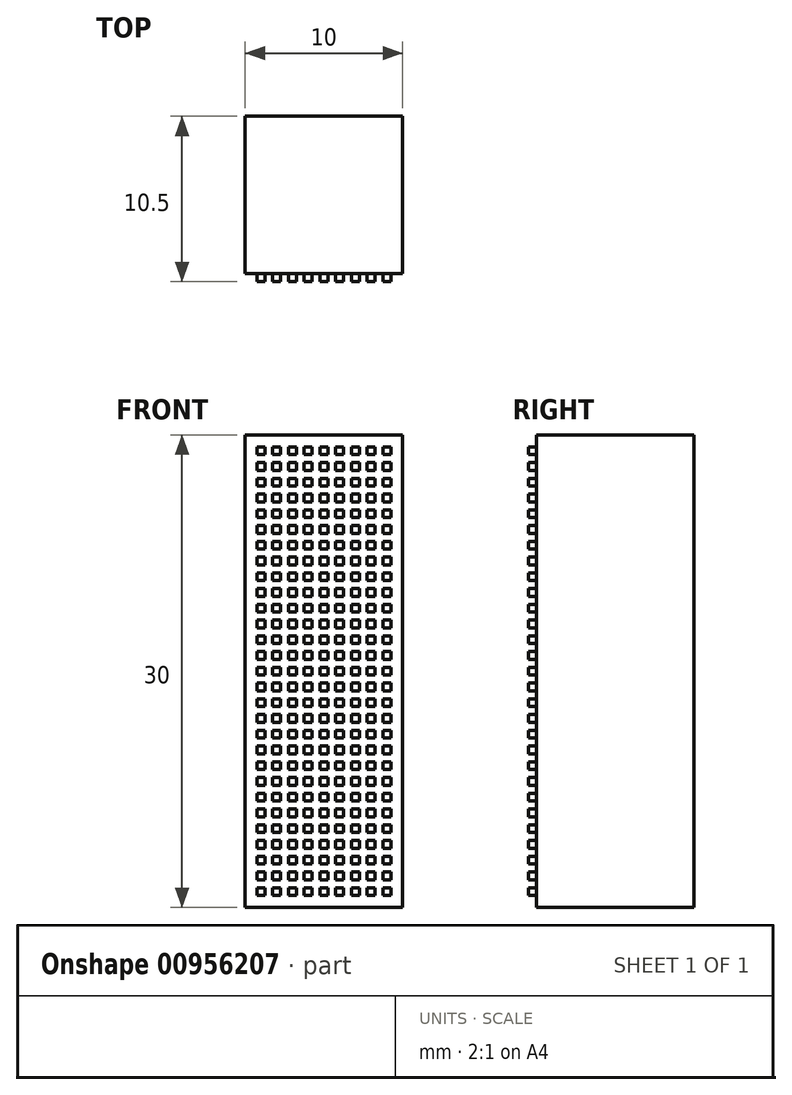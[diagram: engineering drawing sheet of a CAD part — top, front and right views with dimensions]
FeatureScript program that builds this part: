
annotation { "Feature Type Name" : "Feature", "Feature Type Description" : "" }
export const myFeature = defineFeature(function(context is Context, id is Id, definition is map)
    precondition{}
    {
        {
            var Q0;
            Q0=qCreatedBy(makeId("Front.planeOp"),FACE);
            var sketch = newSketch(context, id + "F0", { "sketchPlane" : qUnion([Q0])});
            skLineSegment(sketch, "E0.bottom", {"start": v(0.75, 0.75) * mm, "end": v(1.25, 0.75) * mm});
            skLineSegment(sketch, "E0.top", {"start": v(0.75, 1.25) * mm, "end": v(1.25, 1.25) * mm});
            skLineSegment(sketch, "E0.left", {"start": v(0.75, 0.75) * mm, "end": v(0.75, 1.25) * mm});
            skLineSegment(sketch, "E0.right", {"start": v(1.25, 0.75) * mm, "end": v(1.25, 1.25) * mm});
            skPoint(sketch, "E1", {"position": v(0, 0) * mm});
            skLineSegment(sketch, "E2.1.0.0", {"start": v(1.75, 0.75) * mm, "end": v(1.75, 1.25) * mm});
            skLineSegment(sketch, "E2.1.0.1", {"start": v(1.75, 0.75) * mm, "end": v(2.25, 0.75) * mm});
            skLineSegment(sketch, "E2.1.0.2", {"start": v(1.75, 1.25) * mm, "end": v(2.25, 1.25) * mm});
            skLineSegment(sketch, "E2.1.0.3", {"start": v(2.25, 0.75) * mm, "end": v(2.25, 1.25) * mm});
            skLineSegment(sketch, "E2.2.0.0", {"start": v(2.75, 0.75) * mm, "end": v(2.75, 1.25) * mm});
            skLineSegment(sketch, "E2.2.0.1", {"start": v(2.75, 0.75) * mm, "end": v(3.25, 0.75) * mm});
            skLineSegment(sketch, "E2.2.0.2", {"start": v(2.75, 1.25) * mm, "end": v(3.25, 1.25) * mm});
            skLineSegment(sketch, "E2.2.0.3", {"start": v(3.25, 0.75) * mm, "end": v(3.25, 1.25) * mm});
            skLineSegment(sketch, "E2.3.0.0", {"start": v(3.75, 0.75) * mm, "end": v(3.75, 1.25) * mm});
            skLineSegment(sketch, "E2.3.0.1", {"start": v(3.75, 0.75) * mm, "end": v(4.25, 0.75) * mm});
            skLineSegment(sketch, "E2.3.0.2", {"start": v(3.75, 1.25) * mm, "end": v(4.25, 1.25) * mm});
            skLineSegment(sketch, "E2.3.0.3", {"start": v(4.25, 0.75) * mm, "end": v(4.25, 1.25) * mm});
            skLineSegment(sketch, "E2.4.0.0", {"start": v(4.75, 0.75) * mm, "end": v(4.75, 1.25) * mm});
            skLineSegment(sketch, "E2.4.0.1", {"start": v(4.75, 0.75) * mm, "end": v(5.25, 0.75) * mm});
            skLineSegment(sketch, "E2.4.0.2", {"start": v(4.75, 1.25) * mm, "end": v(5.25, 1.25) * mm});
            skLineSegment(sketch, "E2.4.0.3", {"start": v(5.25, 0.75) * mm, "end": v(5.25, 1.25) * mm});
            skLineSegment(sketch, "E2.5.0.0", {"start": v(5.75, 0.75) * mm, "end": v(5.75, 1.25) * mm});
            skLineSegment(sketch, "E2.5.0.1", {"start": v(5.75, 0.75) * mm, "end": v(6.25, 0.75) * mm});
            skLineSegment(sketch, "E2.5.0.2", {"start": v(5.75, 1.25) * mm, "end": v(6.25, 1.25) * mm});
            skLineSegment(sketch, "E2.5.0.3", {"start": v(6.25, 0.75) * mm, "end": v(6.25, 1.25) * mm});
            skLineSegment(sketch, "E2.6.0.0", {"start": v(6.75, 0.75) * mm, "end": v(6.75, 1.25) * mm});
            skLineSegment(sketch, "E2.6.0.1", {"start": v(6.75, 0.75) * mm, "end": v(7.25, 0.75) * mm});
            skLineSegment(sketch, "E2.6.0.2", {"start": v(6.75, 1.25) * mm, "end": v(7.25, 1.25) * mm});
            skLineSegment(sketch, "E2.6.0.3", {"start": v(7.25, 0.75) * mm, "end": v(7.25, 1.25) * mm});
            skLineSegment(sketch, "E2.7.0.0", {"start": v(7.75, 0.75) * mm, "end": v(7.75, 1.25) * mm});
            skLineSegment(sketch, "E2.7.0.1", {"start": v(7.75, 0.75) * mm, "end": v(8.25, 0.75) * mm});
            skLineSegment(sketch, "E2.7.0.2", {"start": v(7.75, 1.25) * mm, "end": v(8.25, 1.25) * mm});
            skLineSegment(sketch, "E2.7.0.3", {"start": v(8.25, 0.75) * mm, "end": v(8.25, 1.25) * mm});
            skLineSegment(sketch, "E2.8.0.0", {"start": v(8.75, 0.75) * mm, "end": v(8.75, 1.25) * mm});
            skLineSegment(sketch, "E2.8.0.1", {"start": v(8.75, 0.75) * mm, "end": v(9.25, 0.75) * mm});
            skLineSegment(sketch, "E2.8.0.2", {"start": v(8.75, 1.25) * mm, "end": v(9.25, 1.25) * mm});
            skLineSegment(sketch, "E2.8.0.3", {"start": v(9.25, 0.75) * mm, "end": v(9.25, 1.25) * mm});
            skLineSegment(sketch, "E2.direction1", {"start": v(0.75, 0.75) * mm, "end": v(1.75, 0.75) * mm, "construction": true});
            skLineSegment(sketch, "E3.0.1.0", {"start": v(2.75, 2.25) * mm, "end": v(3.25, 2.25) * mm});
            skLineSegment(sketch, "E3.0.1.1", {"start": v(1.25, 1.75) * mm, "end": v(1.25, 2.25) * mm});
            skLineSegment(sketch, "E3.0.1.2", {"start": v(1.75, 2.25) * mm, "end": v(2.25, 2.25) * mm});
            skLineSegment(sketch, "E3.0.1.3", {"start": v(0.75, 1.75) * mm, "end": v(0.75, 2.25) * mm});
            skLineSegment(sketch, "E3.0.1.4", {"start": v(5.75, 2.25) * mm, "end": v(6.25, 2.25) * mm});
            skLineSegment(sketch, "E3.0.1.5", {"start": v(5.25, 1.75) * mm, "end": v(5.25, 2.25) * mm});
            skLineSegment(sketch, "E3.0.1.6", {"start": v(7.75, 1.75) * mm, "end": v(7.75, 2.25) * mm});
            skLineSegment(sketch, "E3.0.1.7", {"start": v(6.75, 1.75) * mm, "end": v(7.25, 1.75) * mm});
            skLineSegment(sketch, "E3.0.1.8", {"start": v(2.75, 1.75) * mm, "end": v(3.25, 1.75) * mm});
            skLineSegment(sketch, "E3.0.1.9", {"start": v(1.75, 1.75) * mm, "end": v(1.75, 2.25) * mm});
            skLineSegment(sketch, "E3.0.1.10", {"start": v(8.75, 1.75) * mm, "end": v(8.75, 2.25) * mm});
            skLineSegment(sketch, "E3.0.1.11", {"start": v(5.75, 1.75) * mm, "end": v(5.75, 2.25) * mm});
            skLineSegment(sketch, "E3.0.1.12", {"start": v(7.25, 1.75) * mm, "end": v(7.25, 2.25) * mm});
            skLineSegment(sketch, "E3.0.1.13", {"start": v(4.25, 1.75) * mm, "end": v(4.25, 2.25) * mm});
            skLineSegment(sketch, "E3.0.1.14", {"start": v(7.75, 2.25) * mm, "end": v(8.25, 2.25) * mm});
            skLineSegment(sketch, "E3.0.1.15", {"start": v(3.75, 1.75) * mm, "end": v(3.75, 2.25) * mm});
            skLineSegment(sketch, "E3.0.1.16", {"start": v(0.75, 2.25) * mm, "end": v(1.25, 2.25) * mm});
            skLineSegment(sketch, "E3.0.1.17", {"start": v(3.75, 1.75) * mm, "end": v(4.25, 1.75) * mm});
            skLineSegment(sketch, "E3.0.1.18", {"start": v(3.75, 2.25) * mm, "end": v(4.25, 2.25) * mm});
            skLineSegment(sketch, "E3.0.1.19", {"start": v(4.75, 1.75) * mm, "end": v(5.25, 1.75) * mm});
            skLineSegment(sketch, "E3.0.1.20", {"start": v(3.25, 1.75) * mm, "end": v(3.25, 2.25) * mm});
            skLineSegment(sketch, "E3.0.1.21", {"start": v(8.75, 1.75) * mm, "end": v(9.25, 1.75) * mm});
            skLineSegment(sketch, "E3.0.1.22", {"start": v(4.75, 2.25) * mm, "end": v(5.25, 2.25) * mm});
            skLineSegment(sketch, "E3.0.1.23", {"start": v(8.75, 2.25) * mm, "end": v(9.25, 2.25) * mm});
            skLineSegment(sketch, "E3.0.1.24", {"start": v(6.75, 1.75) * mm, "end": v(6.75, 2.25) * mm});
            skLineSegment(sketch, "E3.0.1.25", {"start": v(2.75, 1.75) * mm, "end": v(2.75, 2.25) * mm});
            skLineSegment(sketch, "E3.0.1.26", {"start": v(0.75, 1.75) * mm, "end": v(1.75, 1.75) * mm, "construction": true});
            skLineSegment(sketch, "E3.0.1.27", {"start": v(6.25, 1.75) * mm, "end": v(6.25, 2.25) * mm});
            skLineSegment(sketch, "E3.0.1.28", {"start": v(6.75, 2.25) * mm, "end": v(7.25, 2.25) * mm});
            skLineSegment(sketch, "E3.0.1.29", {"start": v(2.25, 1.75) * mm, "end": v(2.25, 2.25) * mm});
            skLineSegment(sketch, "E3.0.1.30", {"start": v(8.25, 1.75) * mm, "end": v(8.25, 2.25) * mm});
            skLineSegment(sketch, "E3.0.1.31", {"start": v(1.75, 1.75) * mm, "end": v(2.25, 1.75) * mm});
            skLineSegment(sketch, "E3.0.1.32", {"start": v(9.25, 1.75) * mm, "end": v(9.25, 2.25) * mm});
            skLineSegment(sketch, "E3.0.1.33", {"start": v(7.75, 1.75) * mm, "end": v(8.25, 1.75) * mm});
            skLineSegment(sketch, "E3.0.1.34", {"start": v(5.75, 1.75) * mm, "end": v(6.25, 1.75) * mm});
            skLineSegment(sketch, "E3.0.1.35", {"start": v(4.75, 1.75) * mm, "end": v(4.75, 2.25) * mm});
            skLineSegment(sketch, "E3.0.1.36", {"start": v(0.75, 1.75) * mm, "end": v(1.25, 1.75) * mm});
            skLineSegment(sketch, "E3.0.2.0", {"start": v(2.75, 3.25) * mm, "end": v(3.25, 3.25) * mm});
            skLineSegment(sketch, "E3.0.2.1", {"start": v(1.25, 2.75) * mm, "end": v(1.25, 3.25) * mm});
            skLineSegment(sketch, "E3.0.2.2", {"start": v(1.75, 3.25) * mm, "end": v(2.25, 3.25) * mm});
            skLineSegment(sketch, "E3.0.2.3", {"start": v(0.75, 2.75) * mm, "end": v(0.75, 3.25) * mm});
            skLineSegment(sketch, "E3.0.2.4", {"start": v(5.75, 3.25) * mm, "end": v(6.25, 3.25) * mm});
            skLineSegment(sketch, "E3.0.2.5", {"start": v(5.25, 2.75) * mm, "end": v(5.25, 3.25) * mm});
            skLineSegment(sketch, "E3.0.2.6", {"start": v(7.75, 2.75) * mm, "end": v(7.75, 3.25) * mm});
            skLineSegment(sketch, "E3.0.2.7", {"start": v(6.75, 2.75) * mm, "end": v(7.25, 2.75) * mm});
            skLineSegment(sketch, "E3.0.2.8", {"start": v(2.75, 2.75) * mm, "end": v(3.25, 2.75) * mm});
            skLineSegment(sketch, "E3.0.2.9", {"start": v(1.75, 2.75) * mm, "end": v(1.75, 3.25) * mm});
            skLineSegment(sketch, "E3.0.2.10", {"start": v(8.75, 2.75) * mm, "end": v(8.75, 3.25) * mm});
            skLineSegment(sketch, "E3.0.2.11", {"start": v(5.75, 2.75) * mm, "end": v(5.75, 3.25) * mm});
            skLineSegment(sketch, "E3.0.2.12", {"start": v(7.25, 2.75) * mm, "end": v(7.25, 3.25) * mm});
            skLineSegment(sketch, "E3.0.2.13", {"start": v(4.25, 2.75) * mm, "end": v(4.25, 3.25) * mm});
            skLineSegment(sketch, "E3.0.2.14", {"start": v(7.75, 3.25) * mm, "end": v(8.25, 3.25) * mm});
            skLineSegment(sketch, "E3.0.2.15", {"start": v(3.75, 2.75) * mm, "end": v(3.75, 3.25) * mm});
            skLineSegment(sketch, "E3.0.2.16", {"start": v(0.75, 3.25) * mm, "end": v(1.25, 3.25) * mm});
            skLineSegment(sketch, "E3.0.2.17", {"start": v(3.75, 2.75) * mm, "end": v(4.25, 2.75) * mm});
            skLineSegment(sketch, "E3.0.2.18", {"start": v(3.75, 3.25) * mm, "end": v(4.25, 3.25) * mm});
            skLineSegment(sketch, "E3.0.2.19", {"start": v(4.75, 2.75) * mm, "end": v(5.25, 2.75) * mm});
            skLineSegment(sketch, "E3.0.2.20", {"start": v(3.25, 2.75) * mm, "end": v(3.25, 3.25) * mm});
            skLineSegment(sketch, "E3.0.2.21", {"start": v(8.75, 2.75) * mm, "end": v(9.25, 2.75) * mm});
            skLineSegment(sketch, "E3.0.2.22", {"start": v(4.75, 3.25) * mm, "end": v(5.25, 3.25) * mm});
            skLineSegment(sketch, "E3.0.2.23", {"start": v(8.75, 3.25) * mm, "end": v(9.25, 3.25) * mm});
            skLineSegment(sketch, "E3.0.2.24", {"start": v(6.75, 2.75) * mm, "end": v(6.75, 3.25) * mm});
            skLineSegment(sketch, "E3.0.2.25", {"start": v(2.75, 2.75) * mm, "end": v(2.75, 3.25) * mm});
            skLineSegment(sketch, "E3.0.2.26", {"start": v(0.75, 2.75) * mm, "end": v(1.75, 2.75) * mm, "construction": true});
            skLineSegment(sketch, "E3.0.2.27", {"start": v(6.25, 2.75) * mm, "end": v(6.25, 3.25) * mm});
            skLineSegment(sketch, "E3.0.2.28", {"start": v(6.75, 3.25) * mm, "end": v(7.25, 3.25) * mm});
            skLineSegment(sketch, "E3.0.2.29", {"start": v(2.25, 2.75) * mm, "end": v(2.25, 3.25) * mm});
            skLineSegment(sketch, "E3.0.2.30", {"start": v(8.25, 2.75) * mm, "end": v(8.25, 3.25) * mm});
            skLineSegment(sketch, "E3.0.2.31", {"start": v(1.75, 2.75) * mm, "end": v(2.25, 2.75) * mm});
            skLineSegment(sketch, "E3.0.2.32", {"start": v(9.25, 2.75) * mm, "end": v(9.25, 3.25) * mm});
            skLineSegment(sketch, "E3.0.2.33", {"start": v(7.75, 2.75) * mm, "end": v(8.25, 2.75) * mm});
            skLineSegment(sketch, "E3.0.2.34", {"start": v(5.75, 2.75) * mm, "end": v(6.25, 2.75) * mm});
            skLineSegment(sketch, "E3.0.2.35", {"start": v(4.75, 2.75) * mm, "end": v(4.75, 3.25) * mm});
            skLineSegment(sketch, "E3.0.2.36", {"start": v(0.75, 2.75) * mm, "end": v(1.25, 2.75) * mm});
            skLineSegment(sketch, "E3.0.3.0", {"start": v(2.75, 4.25) * mm, "end": v(3.25, 4.25) * mm});
            skLineSegment(sketch, "E3.0.3.1", {"start": v(1.25, 3.75) * mm, "end": v(1.25, 4.25) * mm});
            skLineSegment(sketch, "E3.0.3.2", {"start": v(1.75, 4.25) * mm, "end": v(2.25, 4.25) * mm});
            skLineSegment(sketch, "E3.0.3.3", {"start": v(0.75, 3.75) * mm, "end": v(0.75, 4.25) * mm});
            skLineSegment(sketch, "E3.0.3.4", {"start": v(5.75, 4.25) * mm, "end": v(6.25, 4.25) * mm});
            skLineSegment(sketch, "E3.0.3.5", {"start": v(5.25, 3.75) * mm, "end": v(5.25, 4.25) * mm});
            skLineSegment(sketch, "E3.0.3.6", {"start": v(7.75, 3.75) * mm, "end": v(7.75, 4.25) * mm});
            skLineSegment(sketch, "E3.0.3.7", {"start": v(6.75, 3.75) * mm, "end": v(7.25, 3.75) * mm});
            skLineSegment(sketch, "E3.0.3.8", {"start": v(2.75, 3.75) * mm, "end": v(3.25, 3.75) * mm});
            skLineSegment(sketch, "E3.0.3.9", {"start": v(1.75, 3.75) * mm, "end": v(1.75, 4.25) * mm});
            skLineSegment(sketch, "E3.0.3.10", {"start": v(8.75, 3.75) * mm, "end": v(8.75, 4.25) * mm});
            skLineSegment(sketch, "E3.0.3.11", {"start": v(5.75, 3.75) * mm, "end": v(5.75, 4.25) * mm});
            skLineSegment(sketch, "E3.0.3.12", {"start": v(7.25, 3.75) * mm, "end": v(7.25, 4.25) * mm});
            skLineSegment(sketch, "E3.0.3.13", {"start": v(4.25, 3.75) * mm, "end": v(4.25, 4.25) * mm});
            skLineSegment(sketch, "E3.0.3.14", {"start": v(7.75, 4.25) * mm, "end": v(8.25, 4.25) * mm});
            skLineSegment(sketch, "E3.0.3.15", {"start": v(3.75, 3.75) * mm, "end": v(3.75, 4.25) * mm});
            skLineSegment(sketch, "E3.0.3.16", {"start": v(0.75, 4.25) * mm, "end": v(1.25, 4.25) * mm});
            skLineSegment(sketch, "E3.0.3.17", {"start": v(3.75, 3.75) * mm, "end": v(4.25, 3.75) * mm});
            skLineSegment(sketch, "E3.0.3.18", {"start": v(3.75, 4.25) * mm, "end": v(4.25, 4.25) * mm});
            skLineSegment(sketch, "E3.0.3.19", {"start": v(4.75, 3.75) * mm, "end": v(5.25, 3.75) * mm});
            skLineSegment(sketch, "E3.0.3.20", {"start": v(3.25, 3.75) * mm, "end": v(3.25, 4.25) * mm});
            skLineSegment(sketch, "E3.0.3.21", {"start": v(8.75, 3.75) * mm, "end": v(9.25, 3.75) * mm});
            skLineSegment(sketch, "E3.0.3.22", {"start": v(4.75, 4.25) * mm, "end": v(5.25, 4.25) * mm});
            skLineSegment(sketch, "E3.0.3.23", {"start": v(8.75, 4.25) * mm, "end": v(9.25, 4.25) * mm});
            skLineSegment(sketch, "E3.0.3.24", {"start": v(6.75, 3.75) * mm, "end": v(6.75, 4.25) * mm});
            skLineSegment(sketch, "E3.0.3.25", {"start": v(2.75, 3.75) * mm, "end": v(2.75, 4.25) * mm});
            skLineSegment(sketch, "E3.0.3.26", {"start": v(0.75, 3.75) * mm, "end": v(1.75, 3.75) * mm, "construction": true});
            skLineSegment(sketch, "E3.0.3.27", {"start": v(6.25, 3.75) * mm, "end": v(6.25, 4.25) * mm});
            skLineSegment(sketch, "E3.0.3.28", {"start": v(6.75, 4.25) * mm, "end": v(7.25, 4.25) * mm});
            skLineSegment(sketch, "E3.0.3.29", {"start": v(2.25, 3.75) * mm, "end": v(2.25, 4.25) * mm});
            skLineSegment(sketch, "E3.0.3.30", {"start": v(8.25, 3.75) * mm, "end": v(8.25, 4.25) * mm});
            skLineSegment(sketch, "E3.0.3.31", {"start": v(1.75, 3.75) * mm, "end": v(2.25, 3.75) * mm});
            skLineSegment(sketch, "E3.0.3.32", {"start": v(9.25, 3.75) * mm, "end": v(9.25, 4.25) * mm});
            skLineSegment(sketch, "E3.0.3.33", {"start": v(7.75, 3.75) * mm, "end": v(8.25, 3.75) * mm});
            skLineSegment(sketch, "E3.0.3.34", {"start": v(5.75, 3.75) * mm, "end": v(6.25, 3.75) * mm});
            skLineSegment(sketch, "E3.0.3.35", {"start": v(4.75, 3.75) * mm, "end": v(4.75, 4.25) * mm});
            skLineSegment(sketch, "E3.0.3.36", {"start": v(0.75, 3.75) * mm, "end": v(1.25, 3.75) * mm});
            skLineSegment(sketch, "E3.0.4.0", {"start": v(2.75, 5.25) * mm, "end": v(3.25, 5.25) * mm});
            skLineSegment(sketch, "E3.0.4.1", {"start": v(1.25, 4.75) * mm, "end": v(1.25, 5.25) * mm});
            skLineSegment(sketch, "E3.0.4.2", {"start": v(1.75, 5.25) * mm, "end": v(2.25, 5.25) * mm});
            skLineSegment(sketch, "E3.0.4.3", {"start": v(0.75, 4.75) * mm, "end": v(0.75, 5.25) * mm});
            skLineSegment(sketch, "E3.0.4.4", {"start": v(5.75, 5.25) * mm, "end": v(6.25, 5.25) * mm});
            skLineSegment(sketch, "E3.0.4.5", {"start": v(5.25, 4.75) * mm, "end": v(5.25, 5.25) * mm});
            skLineSegment(sketch, "E3.0.4.6", {"start": v(7.75, 4.75) * mm, "end": v(7.75, 5.25) * mm});
            skLineSegment(sketch, "E3.0.4.7", {"start": v(6.75, 4.75) * mm, "end": v(7.25, 4.75) * mm});
            skLineSegment(sketch, "E3.0.4.8", {"start": v(2.75, 4.75) * mm, "end": v(3.25, 4.75) * mm});
            skLineSegment(sketch, "E3.0.4.9", {"start": v(1.75, 4.75) * mm, "end": v(1.75, 5.25) * mm});
            skLineSegment(sketch, "E3.0.4.10", {"start": v(8.75, 4.75) * mm, "end": v(8.75, 5.25) * mm});
            skLineSegment(sketch, "E3.0.4.11", {"start": v(5.75, 4.75) * mm, "end": v(5.75, 5.25) * mm});
            skLineSegment(sketch, "E3.0.4.12", {"start": v(7.25, 4.75) * mm, "end": v(7.25, 5.25) * mm});
            skLineSegment(sketch, "E3.0.4.13", {"start": v(4.25, 4.75) * mm, "end": v(4.25, 5.25) * mm});
            skLineSegment(sketch, "E3.0.4.14", {"start": v(7.75, 5.25) * mm, "end": v(8.25, 5.25) * mm});
            skLineSegment(sketch, "E3.0.4.15", {"start": v(3.75, 4.75) * mm, "end": v(3.75, 5.25) * mm});
            skLineSegment(sketch, "E3.0.4.16", {"start": v(0.75, 5.25) * mm, "end": v(1.25, 5.25) * mm});
            skLineSegment(sketch, "E3.0.4.17", {"start": v(3.75, 4.75) * mm, "end": v(4.25, 4.75) * mm});
            skLineSegment(sketch, "E3.0.4.18", {"start": v(3.75, 5.25) * mm, "end": v(4.25, 5.25) * mm});
            skLineSegment(sketch, "E3.0.4.19", {"start": v(4.75, 4.75) * mm, "end": v(5.25, 4.75) * mm});
            skLineSegment(sketch, "E3.0.4.20", {"start": v(3.25, 4.75) * mm, "end": v(3.25, 5.25) * mm});
            skLineSegment(sketch, "E3.0.4.21", {"start": v(8.75, 4.75) * mm, "end": v(9.25, 4.75) * mm});
            skLineSegment(sketch, "E3.0.4.22", {"start": v(4.75, 5.25) * mm, "end": v(5.25, 5.25) * mm});
            skLineSegment(sketch, "E3.0.4.23", {"start": v(8.75, 5.25) * mm, "end": v(9.25, 5.25) * mm});
            skLineSegment(sketch, "E3.0.4.24", {"start": v(6.75, 4.75) * mm, "end": v(6.75, 5.25) * mm});
            skLineSegment(sketch, "E3.0.4.25", {"start": v(2.75, 4.75) * mm, "end": v(2.75, 5.25) * mm});
            skLineSegment(sketch, "E3.0.4.26", {"start": v(0.75, 4.75) * mm, "end": v(1.75, 4.75) * mm, "construction": true});
            skLineSegment(sketch, "E3.0.4.27", {"start": v(6.25, 4.75) * mm, "end": v(6.25, 5.25) * mm});
            skLineSegment(sketch, "E3.0.4.28", {"start": v(6.75, 5.25) * mm, "end": v(7.25, 5.25) * mm});
            skLineSegment(sketch, "E3.0.4.29", {"start": v(2.25, 4.75) * mm, "end": v(2.25, 5.25) * mm});
            skLineSegment(sketch, "E3.0.4.30", {"start": v(8.25, 4.75) * mm, "end": v(8.25, 5.25) * mm});
            skLineSegment(sketch, "E3.0.4.31", {"start": v(1.75, 4.75) * mm, "end": v(2.25, 4.75) * mm});
            skLineSegment(sketch, "E3.0.4.32", {"start": v(9.25, 4.75) * mm, "end": v(9.25, 5.25) * mm});
            skLineSegment(sketch, "E3.0.4.33", {"start": v(7.75, 4.75) * mm, "end": v(8.25, 4.75) * mm});
            skLineSegment(sketch, "E3.0.4.34", {"start": v(5.75, 4.75) * mm, "end": v(6.25, 4.75) * mm});
            skLineSegment(sketch, "E3.0.4.35", {"start": v(4.75, 4.75) * mm, "end": v(4.75, 5.25) * mm});
            skLineSegment(sketch, "E3.0.4.36", {"start": v(0.75, 4.75) * mm, "end": v(1.25, 4.75) * mm});
            skLineSegment(sketch, "E3.0.5.0", {"start": v(2.75, 6.25) * mm, "end": v(3.25, 6.25) * mm});
            skLineSegment(sketch, "E3.0.5.1", {"start": v(1.25, 5.75) * mm, "end": v(1.25, 6.25) * mm});
            skLineSegment(sketch, "E3.0.5.2", {"start": v(1.75, 6.25) * mm, "end": v(2.25, 6.25) * mm});
            skLineSegment(sketch, "E3.0.5.3", {"start": v(0.75, 5.75) * mm, "end": v(0.75, 6.25) * mm});
            skLineSegment(sketch, "E3.0.5.4", {"start": v(5.75, 6.25) * mm, "end": v(6.25, 6.25) * mm});
            skLineSegment(sketch, "E3.0.5.5", {"start": v(5.25, 5.75) * mm, "end": v(5.25, 6.25) * mm});
            skLineSegment(sketch, "E3.0.5.6", {"start": v(7.75, 5.75) * mm, "end": v(7.75, 6.25) * mm});
            skLineSegment(sketch, "E3.0.5.7", {"start": v(6.75, 5.75) * mm, "end": v(7.25, 5.75) * mm});
            skLineSegment(sketch, "E3.0.5.8", {"start": v(2.75, 5.75) * mm, "end": v(3.25, 5.75) * mm});
            skLineSegment(sketch, "E3.0.5.9", {"start": v(1.75, 5.75) * mm, "end": v(1.75, 6.25) * mm});
            skLineSegment(sketch, "E3.0.5.10", {"start": v(8.75, 5.75) * mm, "end": v(8.75, 6.25) * mm});
            skLineSegment(sketch, "E3.0.5.11", {"start": v(5.75, 5.75) * mm, "end": v(5.75, 6.25) * mm});
            skLineSegment(sketch, "E3.0.5.12", {"start": v(7.25, 5.75) * mm, "end": v(7.25, 6.25) * mm});
            skLineSegment(sketch, "E3.0.5.13", {"start": v(4.25, 5.75) * mm, "end": v(4.25, 6.25) * mm});
            skLineSegment(sketch, "E3.0.5.14", {"start": v(7.75, 6.25) * mm, "end": v(8.25, 6.25) * mm});
            skLineSegment(sketch, "E3.0.5.15", {"start": v(3.75, 5.75) * mm, "end": v(3.75, 6.25) * mm});
            skLineSegment(sketch, "E3.0.5.16", {"start": v(0.75, 6.25) * mm, "end": v(1.25, 6.25) * mm});
            skLineSegment(sketch, "E3.0.5.17", {"start": v(3.75, 5.75) * mm, "end": v(4.25, 5.75) * mm});
            skLineSegment(sketch, "E3.0.5.18", {"start": v(3.75, 6.25) * mm, "end": v(4.25, 6.25) * mm});
            skLineSegment(sketch, "E3.0.5.19", {"start": v(4.75, 5.75) * mm, "end": v(5.25, 5.75) * mm});
            skLineSegment(sketch, "E3.0.5.20", {"start": v(3.25, 5.75) * mm, "end": v(3.25, 6.25) * mm});
            skLineSegment(sketch, "E3.0.5.21", {"start": v(8.75, 5.75) * mm, "end": v(9.25, 5.75) * mm});
            skLineSegment(sketch, "E3.0.5.22", {"start": v(4.75, 6.25) * mm, "end": v(5.25, 6.25) * mm});
            skLineSegment(sketch, "E3.0.5.23", {"start": v(8.75, 6.25) * mm, "end": v(9.25, 6.25) * mm});
            skLineSegment(sketch, "E3.0.5.24", {"start": v(6.75, 5.75) * mm, "end": v(6.75, 6.25) * mm});
            skLineSegment(sketch, "E3.0.5.25", {"start": v(2.75, 5.75) * mm, "end": v(2.75, 6.25) * mm});
            skLineSegment(sketch, "E3.0.5.26", {"start": v(0.75, 5.75) * mm, "end": v(1.75, 5.75) * mm, "construction": true});
            skLineSegment(sketch, "E3.0.5.27", {"start": v(6.25, 5.75) * mm, "end": v(6.25, 6.25) * mm});
            skLineSegment(sketch, "E3.0.5.28", {"start": v(6.75, 6.25) * mm, "end": v(7.25, 6.25) * mm});
            skLineSegment(sketch, "E3.0.5.29", {"start": v(2.25, 5.75) * mm, "end": v(2.25, 6.25) * mm});
            skLineSegment(sketch, "E3.0.5.30", {"start": v(8.25, 5.75) * mm, "end": v(8.25, 6.25) * mm});
            skLineSegment(sketch, "E3.0.5.31", {"start": v(1.75, 5.75) * mm, "end": v(2.25, 5.75) * mm});
            skLineSegment(sketch, "E3.0.5.32", {"start": v(9.25, 5.75) * mm, "end": v(9.25, 6.25) * mm});
            skLineSegment(sketch, "E3.0.5.33", {"start": v(7.75, 5.75) * mm, "end": v(8.25, 5.75) * mm});
            skLineSegment(sketch, "E3.0.5.34", {"start": v(5.75, 5.75) * mm, "end": v(6.25, 5.75) * mm});
            skLineSegment(sketch, "E3.0.5.35", {"start": v(4.75, 5.75) * mm, "end": v(4.75, 6.25) * mm});
            skLineSegment(sketch, "E3.0.5.36", {"start": v(0.75, 5.75) * mm, "end": v(1.25, 5.75) * mm});
            skLineSegment(sketch, "E3.0.6.0", {"start": v(2.75, 7.25) * mm, "end": v(3.25, 7.25) * mm});
            skLineSegment(sketch, "E3.0.6.1", {"start": v(1.25, 6.75) * mm, "end": v(1.25, 7.25) * mm});
            skLineSegment(sketch, "E3.0.6.2", {"start": v(1.75, 7.25) * mm, "end": v(2.25, 7.25) * mm});
            skLineSegment(sketch, "E3.0.6.3", {"start": v(0.75, 6.75) * mm, "end": v(0.75, 7.25) * mm});
            skLineSegment(sketch, "E3.0.6.4", {"start": v(5.75, 7.25) * mm, "end": v(6.25, 7.25) * mm});
            skLineSegment(sketch, "E3.0.6.5", {"start": v(5.25, 6.75) * mm, "end": v(5.25, 7.25) * mm});
            skLineSegment(sketch, "E3.0.6.6", {"start": v(7.75, 6.75) * mm, "end": v(7.75, 7.25) * mm});
            skLineSegment(sketch, "E3.0.6.7", {"start": v(6.75, 6.75) * mm, "end": v(7.25, 6.75) * mm});
            skLineSegment(sketch, "E3.0.6.8", {"start": v(2.75, 6.75) * mm, "end": v(3.25, 6.75) * mm});
            skLineSegment(sketch, "E3.0.6.9", {"start": v(1.75, 6.75) * mm, "end": v(1.75, 7.25) * mm});
            skLineSegment(sketch, "E3.0.6.10", {"start": v(8.75, 6.75) * mm, "end": v(8.75, 7.25) * mm});
            skLineSegment(sketch, "E3.0.6.11", {"start": v(5.75, 6.75) * mm, "end": v(5.75, 7.25) * mm});
            skLineSegment(sketch, "E3.0.6.12", {"start": v(7.25, 6.75) * mm, "end": v(7.25, 7.25) * mm});
            skLineSegment(sketch, "E3.0.6.13", {"start": v(4.25, 6.75) * mm, "end": v(4.25, 7.25) * mm});
            skLineSegment(sketch, "E3.0.6.14", {"start": v(7.75, 7.25) * mm, "end": v(8.25, 7.25) * mm});
            skLineSegment(sketch, "E3.0.6.15", {"start": v(3.75, 6.75) * mm, "end": v(3.75, 7.25) * mm});
            skLineSegment(sketch, "E3.0.6.16", {"start": v(0.75, 7.25) * mm, "end": v(1.25, 7.25) * mm});
            skLineSegment(sketch, "E3.0.6.17", {"start": v(3.75, 6.75) * mm, "end": v(4.25, 6.75) * mm});
            skLineSegment(sketch, "E3.0.6.18", {"start": v(3.75, 7.25) * mm, "end": v(4.25, 7.25) * mm});
            skLineSegment(sketch, "E3.0.6.19", {"start": v(4.75, 6.75) * mm, "end": v(5.25, 6.75) * mm});
            skLineSegment(sketch, "E3.0.6.20", {"start": v(3.25, 6.75) * mm, "end": v(3.25, 7.25) * mm});
            skLineSegment(sketch, "E3.0.6.21", {"start": v(8.75, 6.75) * mm, "end": v(9.25, 6.75) * mm});
            skLineSegment(sketch, "E3.0.6.22", {"start": v(4.75, 7.25) * mm, "end": v(5.25, 7.25) * mm});
            skLineSegment(sketch, "E3.0.6.23", {"start": v(8.75, 7.25) * mm, "end": v(9.25, 7.25) * mm});
            skLineSegment(sketch, "E3.0.6.24", {"start": v(6.75, 6.75) * mm, "end": v(6.75, 7.25) * mm});
            skLineSegment(sketch, "E3.0.6.25", {"start": v(2.75, 6.75) * mm, "end": v(2.75, 7.25) * mm});
            skLineSegment(sketch, "E3.0.6.26", {"start": v(0.75, 6.75) * mm, "end": v(1.75, 6.75) * mm, "construction": true});
            skLineSegment(sketch, "E3.0.6.27", {"start": v(6.25, 6.75) * mm, "end": v(6.25, 7.25) * mm});
            skLineSegment(sketch, "E3.0.6.28", {"start": v(6.75, 7.25) * mm, "end": v(7.25, 7.25) * mm});
            skLineSegment(sketch, "E3.0.6.29", {"start": v(2.25, 6.75) * mm, "end": v(2.25, 7.25) * mm});
            skLineSegment(sketch, "E3.0.6.30", {"start": v(8.25, 6.75) * mm, "end": v(8.25, 7.25) * mm});
            skLineSegment(sketch, "E3.0.6.31", {"start": v(1.75, 6.75) * mm, "end": v(2.25, 6.75) * mm});
            skLineSegment(sketch, "E3.0.6.32", {"start": v(9.25, 6.75) * mm, "end": v(9.25, 7.25) * mm});
            skLineSegment(sketch, "E3.0.6.33", {"start": v(7.75, 6.75) * mm, "end": v(8.25, 6.75) * mm});
            skLineSegment(sketch, "E3.0.6.34", {"start": v(5.75, 6.75) * mm, "end": v(6.25, 6.75) * mm});
            skLineSegment(sketch, "E3.0.6.35", {"start": v(4.75, 6.75) * mm, "end": v(4.75, 7.25) * mm});
            skLineSegment(sketch, "E3.0.6.36", {"start": v(0.75, 6.75) * mm, "end": v(1.25, 6.75) * mm});
            skLineSegment(sketch, "E3.0.7.0", {"start": v(2.75, 8.25) * mm, "end": v(3.25, 8.25) * mm});
            skLineSegment(sketch, "E3.0.7.1", {"start": v(1.25, 7.75) * mm, "end": v(1.25, 8.25) * mm});
            skLineSegment(sketch, "E3.0.7.2", {"start": v(1.75, 8.25) * mm, "end": v(2.25, 8.25) * mm});
            skLineSegment(sketch, "E3.0.7.3", {"start": v(0.75, 7.75) * mm, "end": v(0.75, 8.25) * mm});
            skLineSegment(sketch, "E3.0.7.4", {"start": v(5.75, 8.25) * mm, "end": v(6.25, 8.25) * mm});
            skLineSegment(sketch, "E3.0.7.5", {"start": v(5.25, 7.75) * mm, "end": v(5.25, 8.25) * mm});
            skLineSegment(sketch, "E3.0.7.6", {"start": v(7.75, 7.75) * mm, "end": v(7.75, 8.25) * mm});
            skLineSegment(sketch, "E3.0.7.7", {"start": v(6.75, 7.75) * mm, "end": v(7.25, 7.75) * mm});
            skLineSegment(sketch, "E3.0.7.8", {"start": v(2.75, 7.75) * mm, "end": v(3.25, 7.75) * mm});
            skLineSegment(sketch, "E3.0.7.9", {"start": v(1.75, 7.75) * mm, "end": v(1.75, 8.25) * mm});
            skLineSegment(sketch, "E3.0.7.10", {"start": v(8.75, 7.75) * mm, "end": v(8.75, 8.25) * mm});
            skLineSegment(sketch, "E3.0.7.11", {"start": v(5.75, 7.75) * mm, "end": v(5.75, 8.25) * mm});
            skLineSegment(sketch, "E3.0.7.12", {"start": v(7.25, 7.75) * mm, "end": v(7.25, 8.25) * mm});
            skLineSegment(sketch, "E3.0.7.13", {"start": v(4.25, 7.75) * mm, "end": v(4.25, 8.25) * mm});
            skLineSegment(sketch, "E3.0.7.14", {"start": v(7.75, 8.25) * mm, "end": v(8.25, 8.25) * mm});
            skLineSegment(sketch, "E3.0.7.15", {"start": v(3.75, 7.75) * mm, "end": v(3.75, 8.25) * mm});
            skLineSegment(sketch, "E3.0.7.16", {"start": v(0.75, 8.25) * mm, "end": v(1.25, 8.25) * mm});
            skLineSegment(sketch, "E3.0.7.17", {"start": v(3.75, 7.75) * mm, "end": v(4.25, 7.75) * mm});
            skLineSegment(sketch, "E3.0.7.18", {"start": v(3.75, 8.25) * mm, "end": v(4.25, 8.25) * mm});
            skLineSegment(sketch, "E3.0.7.19", {"start": v(4.75, 7.75) * mm, "end": v(5.25, 7.75) * mm});
            skLineSegment(sketch, "E3.0.7.20", {"start": v(3.25, 7.75) * mm, "end": v(3.25, 8.25) * mm});
            skLineSegment(sketch, "E3.0.7.21", {"start": v(8.75, 7.75) * mm, "end": v(9.25, 7.75) * mm});
            skLineSegment(sketch, "E3.0.7.22", {"start": v(4.75, 8.25) * mm, "end": v(5.25, 8.25) * mm});
            skLineSegment(sketch, "E3.0.7.23", {"start": v(8.75, 8.25) * mm, "end": v(9.25, 8.25) * mm});
            skLineSegment(sketch, "E3.0.7.24", {"start": v(6.75, 7.75) * mm, "end": v(6.75, 8.25) * mm});
            skLineSegment(sketch, "E3.0.7.25", {"start": v(2.75, 7.75) * mm, "end": v(2.75, 8.25) * mm});
            skLineSegment(sketch, "E3.0.7.26", {"start": v(0.75, 7.75) * mm, "end": v(1.75, 7.75) * mm, "construction": true});
            skLineSegment(sketch, "E3.0.7.27", {"start": v(6.25, 7.75) * mm, "end": v(6.25, 8.25) * mm});
            skLineSegment(sketch, "E3.0.7.28", {"start": v(6.75, 8.25) * mm, "end": v(7.25, 8.25) * mm});
            skLineSegment(sketch, "E3.0.7.29", {"start": v(2.25, 7.75) * mm, "end": v(2.25, 8.25) * mm});
            skLineSegment(sketch, "E3.0.7.30", {"start": v(8.25, 7.75) * mm, "end": v(8.25, 8.25) * mm});
            skLineSegment(sketch, "E3.0.7.31", {"start": v(1.75, 7.75) * mm, "end": v(2.25, 7.75) * mm});
            skLineSegment(sketch, "E3.0.7.32", {"start": v(9.25, 7.75) * mm, "end": v(9.25, 8.25) * mm});
            skLineSegment(sketch, "E3.0.7.33", {"start": v(7.75, 7.75) * mm, "end": v(8.25, 7.75) * mm});
            skLineSegment(sketch, "E3.0.7.34", {"start": v(5.75, 7.75) * mm, "end": v(6.25, 7.75) * mm});
            skLineSegment(sketch, "E3.0.7.35", {"start": v(4.75, 7.75) * mm, "end": v(4.75, 8.25) * mm});
            skLineSegment(sketch, "E3.0.7.36", {"start": v(0.75, 7.75) * mm, "end": v(1.25, 7.75) * mm});
            skLineSegment(sketch, "E3.0.8.0", {"start": v(2.75, 9.25) * mm, "end": v(3.25, 9.25) * mm});
            skLineSegment(sketch, "E3.0.8.1", {"start": v(1.25, 8.75) * mm, "end": v(1.25, 9.25) * mm});
            skLineSegment(sketch, "E3.0.8.2", {"start": v(1.75, 9.25) * mm, "end": v(2.25, 9.25) * mm});
            skLineSegment(sketch, "E3.0.8.3", {"start": v(0.75, 8.75) * mm, "end": v(0.75, 9.25) * mm});
            skLineSegment(sketch, "E3.0.8.4", {"start": v(5.75, 9.25) * mm, "end": v(6.25, 9.25) * mm});
            skLineSegment(sketch, "E3.0.8.5", {"start": v(5.25, 8.75) * mm, "end": v(5.25, 9.25) * mm});
            skLineSegment(sketch, "E3.0.8.6", {"start": v(7.75, 8.75) * mm, "end": v(7.75, 9.25) * mm});
            skLineSegment(sketch, "E3.0.8.7", {"start": v(6.75, 8.75) * mm, "end": v(7.25, 8.75) * mm});
            skLineSegment(sketch, "E3.0.8.8", {"start": v(2.75, 8.75) * mm, "end": v(3.25, 8.75) * mm});
            skLineSegment(sketch, "E3.0.8.9", {"start": v(1.75, 8.75) * mm, "end": v(1.75, 9.25) * mm});
            skLineSegment(sketch, "E3.0.8.10", {"start": v(8.75, 8.75) * mm, "end": v(8.75, 9.25) * mm});
            skLineSegment(sketch, "E3.0.8.11", {"start": v(5.75, 8.75) * mm, "end": v(5.75, 9.25) * mm});
            skLineSegment(sketch, "E3.0.8.12", {"start": v(7.25, 8.75) * mm, "end": v(7.25, 9.25) * mm});
            skLineSegment(sketch, "E3.0.8.13", {"start": v(4.25, 8.75) * mm, "end": v(4.25, 9.25) * mm});
            skLineSegment(sketch, "E3.0.8.14", {"start": v(7.75, 9.25) * mm, "end": v(8.25, 9.25) * mm});
            skLineSegment(sketch, "E3.0.8.15", {"start": v(3.75, 8.75) * mm, "end": v(3.75, 9.25) * mm});
            skLineSegment(sketch, "E3.0.8.16", {"start": v(0.75, 9.25) * mm, "end": v(1.25, 9.25) * mm});
            skLineSegment(sketch, "E3.0.8.17", {"start": v(3.75, 8.75) * mm, "end": v(4.25, 8.75) * mm});
            skLineSegment(sketch, "E3.0.8.18", {"start": v(3.75, 9.25) * mm, "end": v(4.25, 9.25) * mm});
            skLineSegment(sketch, "E3.0.8.19", {"start": v(4.75, 8.75) * mm, "end": v(5.25, 8.75) * mm});
            skLineSegment(sketch, "E3.0.8.20", {"start": v(3.25, 8.75) * mm, "end": v(3.25, 9.25) * mm});
            skLineSegment(sketch, "E3.0.8.21", {"start": v(8.75, 8.75) * mm, "end": v(9.25, 8.75) * mm});
            skLineSegment(sketch, "E3.0.8.22", {"start": v(4.75, 9.25) * mm, "end": v(5.25, 9.25) * mm});
            skLineSegment(sketch, "E3.0.8.23", {"start": v(8.75, 9.25) * mm, "end": v(9.25, 9.25) * mm});
            skLineSegment(sketch, "E3.0.8.24", {"start": v(6.75, 8.75) * mm, "end": v(6.75, 9.25) * mm});
            skLineSegment(sketch, "E3.0.8.25", {"start": v(2.75, 8.75) * mm, "end": v(2.75, 9.25) * mm});
            skLineSegment(sketch, "E3.0.8.26", {"start": v(0.75, 8.75) * mm, "end": v(1.75, 8.75) * mm, "construction": true});
            skLineSegment(sketch, "E3.0.8.27", {"start": v(6.25, 8.75) * mm, "end": v(6.25, 9.25) * mm});
            skLineSegment(sketch, "E3.0.8.28", {"start": v(6.75, 9.25) * mm, "end": v(7.25, 9.25) * mm});
            skLineSegment(sketch, "E3.0.8.29", {"start": v(2.25, 8.75) * mm, "end": v(2.25, 9.25) * mm});
            skLineSegment(sketch, "E3.0.8.30", {"start": v(8.25, 8.75) * mm, "end": v(8.25, 9.25) * mm});
            skLineSegment(sketch, "E3.0.8.31", {"start": v(1.75, 8.75) * mm, "end": v(2.25, 8.75) * mm});
            skLineSegment(sketch, "E3.0.8.32", {"start": v(9.25, 8.75) * mm, "end": v(9.25, 9.25) * mm});
            skLineSegment(sketch, "E3.0.8.33", {"start": v(7.75, 8.75) * mm, "end": v(8.25, 8.75) * mm});
            skLineSegment(sketch, "E3.0.8.34", {"start": v(5.75, 8.75) * mm, "end": v(6.25, 8.75) * mm});
            skLineSegment(sketch, "E3.0.8.35", {"start": v(4.75, 8.75) * mm, "end": v(4.75, 9.25) * mm});
            skLineSegment(sketch, "E3.0.8.36", {"start": v(0.75, 8.75) * mm, "end": v(1.25, 8.75) * mm});
            skLineSegment(sketch, "E3.0.9.0", {"start": v(2.75, 10.25) * mm, "end": v(3.25, 10.25) * mm});
            skLineSegment(sketch, "E3.0.9.1", {"start": v(1.25, 9.75) * mm, "end": v(1.25, 10.25) * mm});
            skLineSegment(sketch, "E3.0.9.2", {"start": v(1.75, 10.25) * mm, "end": v(2.25, 10.25) * mm});
            skLineSegment(sketch, "E3.0.9.3", {"start": v(0.75, 9.75) * mm, "end": v(0.75, 10.25) * mm});
            skLineSegment(sketch, "E3.0.9.4", {"start": v(5.75, 10.25) * mm, "end": v(6.25, 10.25) * mm});
            skLineSegment(sketch, "E3.0.9.5", {"start": v(5.25, 9.75) * mm, "end": v(5.25, 10.25) * mm});
            skLineSegment(sketch, "E3.0.9.6", {"start": v(7.75, 9.75) * mm, "end": v(7.75, 10.25) * mm});
            skLineSegment(sketch, "E3.0.9.7", {"start": v(6.75, 9.75) * mm, "end": v(7.25, 9.75) * mm});
            skLineSegment(sketch, "E3.0.9.8", {"start": v(2.75, 9.75) * mm, "end": v(3.25, 9.75) * mm});
            skLineSegment(sketch, "E3.0.9.9", {"start": v(1.75, 9.75) * mm, "end": v(1.75, 10.25) * mm});
            skLineSegment(sketch, "E3.0.9.10", {"start": v(8.75, 9.75) * mm, "end": v(8.75, 10.25) * mm});
            skLineSegment(sketch, "E3.0.9.11", {"start": v(5.75, 9.75) * mm, "end": v(5.75, 10.25) * mm});
            skLineSegment(sketch, "E3.0.9.12", {"start": v(7.25, 9.75) * mm, "end": v(7.25, 10.25) * mm});
            skLineSegment(sketch, "E3.0.9.13", {"start": v(4.25, 9.75) * mm, "end": v(4.25, 10.25) * mm});
            skLineSegment(sketch, "E3.0.9.14", {"start": v(7.75, 10.25) * mm, "end": v(8.25, 10.25) * mm});
            skLineSegment(sketch, "E3.0.9.15", {"start": v(3.75, 9.75) * mm, "end": v(3.75, 10.25) * mm});
            skLineSegment(sketch, "E3.0.9.16", {"start": v(0.75, 10.25) * mm, "end": v(1.25, 10.25) * mm});
            skLineSegment(sketch, "E3.0.9.17", {"start": v(3.75, 9.75) * mm, "end": v(4.25, 9.75) * mm});
            skLineSegment(sketch, "E3.0.9.18", {"start": v(3.75, 10.25) * mm, "end": v(4.25, 10.25) * mm});
            skLineSegment(sketch, "E3.0.9.19", {"start": v(4.75, 9.75) * mm, "end": v(5.25, 9.75) * mm});
            skLineSegment(sketch, "E3.0.9.20", {"start": v(3.25, 9.75) * mm, "end": v(3.25, 10.25) * mm});
            skLineSegment(sketch, "E3.0.9.21", {"start": v(8.75, 9.75) * mm, "end": v(9.25, 9.75) * mm});
            skLineSegment(sketch, "E3.0.9.22", {"start": v(4.75, 10.25) * mm, "end": v(5.25, 10.25) * mm});
            skLineSegment(sketch, "E3.0.9.23", {"start": v(8.75, 10.25) * mm, "end": v(9.25, 10.25) * mm});
            skLineSegment(sketch, "E3.0.9.24", {"start": v(6.75, 9.75) * mm, "end": v(6.75, 10.25) * mm});
            skLineSegment(sketch, "E3.0.9.25", {"start": v(2.75, 9.75) * mm, "end": v(2.75, 10.25) * mm});
            skLineSegment(sketch, "E3.0.9.26", {"start": v(0.75, 9.75) * mm, "end": v(1.75, 9.75) * mm, "construction": true});
            skLineSegment(sketch, "E3.0.9.27", {"start": v(6.25, 9.75) * mm, "end": v(6.25, 10.25) * mm});
            skLineSegment(sketch, "E3.0.9.28", {"start": v(6.75, 10.25) * mm, "end": v(7.25, 10.25) * mm});
            skLineSegment(sketch, "E3.0.9.29", {"start": v(2.25, 9.75) * mm, "end": v(2.25, 10.25) * mm});
            skLineSegment(sketch, "E3.0.9.30", {"start": v(8.25, 9.75) * mm, "end": v(8.25, 10.25) * mm});
            skLineSegment(sketch, "E3.0.9.31", {"start": v(1.75, 9.75) * mm, "end": v(2.25, 9.75) * mm});
            skLineSegment(sketch, "E3.0.9.32", {"start": v(9.25, 9.75) * mm, "end": v(9.25, 10.25) * mm});
            skLineSegment(sketch, "E3.0.9.33", {"start": v(7.75, 9.75) * mm, "end": v(8.25, 9.75) * mm});
            skLineSegment(sketch, "E3.0.9.34", {"start": v(5.75, 9.75) * mm, "end": v(6.25, 9.75) * mm});
            skLineSegment(sketch, "E3.0.9.35", {"start": v(4.75, 9.75) * mm, "end": v(4.75, 10.25) * mm});
            skLineSegment(sketch, "E3.0.9.36", {"start": v(0.75, 9.75) * mm, "end": v(1.25, 9.75) * mm});
            skLineSegment(sketch, "E3.0.10.0", {"start": v(2.75, 11.25) * mm, "end": v(3.25, 11.25) * mm});
            skLineSegment(sketch, "E3.0.10.1", {"start": v(1.25, 10.75) * mm, "end": v(1.25, 11.25) * mm});
            skLineSegment(sketch, "E3.0.10.2", {"start": v(1.75, 11.25) * mm, "end": v(2.25, 11.25) * mm});
            skLineSegment(sketch, "E3.0.10.3", {"start": v(0.75, 10.75) * mm, "end": v(0.75, 11.25) * mm});
            skLineSegment(sketch, "E3.0.10.4", {"start": v(5.75, 11.25) * mm, "end": v(6.25, 11.25) * mm});
            skLineSegment(sketch, "E3.0.10.5", {"start": v(5.25, 10.75) * mm, "end": v(5.25, 11.25) * mm});
            skLineSegment(sketch, "E3.0.10.6", {"start": v(7.75, 10.75) * mm, "end": v(7.75, 11.25) * mm});
            skLineSegment(sketch, "E3.0.10.7", {"start": v(6.75, 10.75) * mm, "end": v(7.25, 10.75) * mm});
            skLineSegment(sketch, "E3.0.10.8", {"start": v(2.75, 10.75) * mm, "end": v(3.25, 10.75) * mm});
            skLineSegment(sketch, "E3.0.10.9", {"start": v(1.75, 10.75) * mm, "end": v(1.75, 11.25) * mm});
            skLineSegment(sketch, "E3.0.10.10", {"start": v(8.75, 10.75) * mm, "end": v(8.75, 11.25) * mm});
            skLineSegment(sketch, "E3.0.10.11", {"start": v(5.75, 10.75) * mm, "end": v(5.75, 11.25) * mm});
            skLineSegment(sketch, "E3.0.10.12", {"start": v(7.25, 10.75) * mm, "end": v(7.25, 11.25) * mm});
            skLineSegment(sketch, "E3.0.10.13", {"start": v(4.25, 10.75) * mm, "end": v(4.25, 11.25) * mm});
            skLineSegment(sketch, "E3.0.10.14", {"start": v(7.75, 11.25) * mm, "end": v(8.25, 11.25) * mm});
            skLineSegment(sketch, "E3.0.10.15", {"start": v(3.75, 10.75) * mm, "end": v(3.75, 11.25) * mm});
            skLineSegment(sketch, "E3.0.10.16", {"start": v(0.75, 11.25) * mm, "end": v(1.25, 11.25) * mm});
            skLineSegment(sketch, "E3.0.10.17", {"start": v(3.75, 10.75) * mm, "end": v(4.25, 10.75) * mm});
            skLineSegment(sketch, "E3.0.10.18", {"start": v(3.75, 11.25) * mm, "end": v(4.25, 11.25) * mm});
            skLineSegment(sketch, "E3.0.10.19", {"start": v(4.75, 10.75) * mm, "end": v(5.25, 10.75) * mm});
            skLineSegment(sketch, "E3.0.10.20", {"start": v(3.25, 10.75) * mm, "end": v(3.25, 11.25) * mm});
            skLineSegment(sketch, "E3.0.10.21", {"start": v(8.75, 10.75) * mm, "end": v(9.25, 10.75) * mm});
            skLineSegment(sketch, "E3.0.10.22", {"start": v(4.75, 11.25) * mm, "end": v(5.25, 11.25) * mm});
            skLineSegment(sketch, "E3.0.10.23", {"start": v(8.75, 11.25) * mm, "end": v(9.25, 11.25) * mm});
            skLineSegment(sketch, "E3.0.10.24", {"start": v(6.75, 10.75) * mm, "end": v(6.75, 11.25) * mm});
            skLineSegment(sketch, "E3.0.10.25", {"start": v(2.75, 10.75) * mm, "end": v(2.75, 11.25) * mm});
            skLineSegment(sketch, "E3.0.10.26", {"start": v(0.75, 10.75) * mm, "end": v(1.75, 10.75) * mm, "construction": true});
            skLineSegment(sketch, "E3.0.10.27", {"start": v(6.25, 10.75) * mm, "end": v(6.25, 11.25) * mm});
            skLineSegment(sketch, "E3.0.10.28", {"start": v(6.75, 11.25) * mm, "end": v(7.25, 11.25) * mm});
            skLineSegment(sketch, "E3.0.10.29", {"start": v(2.25, 10.75) * mm, "end": v(2.25, 11.25) * mm});
            skLineSegment(sketch, "E3.0.10.30", {"start": v(8.25, 10.75) * mm, "end": v(8.25, 11.25) * mm});
            skLineSegment(sketch, "E3.0.10.31", {"start": v(1.75, 10.75) * mm, "end": v(2.25, 10.75) * mm});
            skLineSegment(sketch, "E3.0.10.32", {"start": v(9.25, 10.75) * mm, "end": v(9.25, 11.25) * mm});
            skLineSegment(sketch, "E3.0.10.33", {"start": v(7.75, 10.75) * mm, "end": v(8.25, 10.75) * mm});
            skLineSegment(sketch, "E3.0.10.34", {"start": v(5.75, 10.75) * mm, "end": v(6.25, 10.75) * mm});
            skLineSegment(sketch, "E3.0.10.35", {"start": v(4.75, 10.75) * mm, "end": v(4.75, 11.25) * mm});
            skLineSegment(sketch, "E3.0.10.36", {"start": v(0.75, 10.75) * mm, "end": v(1.25, 10.75) * mm});
            skLineSegment(sketch, "E3.0.11.0", {"start": v(2.75, 12.25) * mm, "end": v(3.25, 12.25) * mm});
            skLineSegment(sketch, "E3.0.11.1", {"start": v(1.25, 11.75) * mm, "end": v(1.25, 12.25) * mm});
            skLineSegment(sketch, "E3.0.11.2", {"start": v(1.75, 12.25) * mm, "end": v(2.25, 12.25) * mm});
            skLineSegment(sketch, "E3.0.11.3", {"start": v(0.75, 11.75) * mm, "end": v(0.75, 12.25) * mm});
            skLineSegment(sketch, "E3.0.11.4", {"start": v(5.75, 12.25) * mm, "end": v(6.25, 12.25) * mm});
            skLineSegment(sketch, "E3.0.11.5", {"start": v(5.25, 11.75) * mm, "end": v(5.25, 12.25) * mm});
            skLineSegment(sketch, "E3.0.11.6", {"start": v(7.75, 11.75) * mm, "end": v(7.75, 12.25) * mm});
            skLineSegment(sketch, "E3.0.11.7", {"start": v(6.75, 11.75) * mm, "end": v(7.25, 11.75) * mm});
            skLineSegment(sketch, "E3.0.11.8", {"start": v(2.75, 11.75) * mm, "end": v(3.25, 11.75) * mm});
            skLineSegment(sketch, "E3.0.11.9", {"start": v(1.75, 11.75) * mm, "end": v(1.75, 12.25) * mm});
            skLineSegment(sketch, "E3.0.11.10", {"start": v(8.75, 11.75) * mm, "end": v(8.75, 12.25) * mm});
            skLineSegment(sketch, "E3.0.11.11", {"start": v(5.75, 11.75) * mm, "end": v(5.75, 12.25) * mm});
            skLineSegment(sketch, "E3.0.11.12", {"start": v(7.25, 11.75) * mm, "end": v(7.25, 12.25) * mm});
            skLineSegment(sketch, "E3.0.11.13", {"start": v(4.25, 11.75) * mm, "end": v(4.25, 12.25) * mm});
            skLineSegment(sketch, "E3.0.11.14", {"start": v(7.75, 12.25) * mm, "end": v(8.25, 12.25) * mm});
            skLineSegment(sketch, "E3.0.11.15", {"start": v(3.75, 11.75) * mm, "end": v(3.75, 12.25) * mm});
            skLineSegment(sketch, "E3.0.11.16", {"start": v(0.75, 12.25) * mm, "end": v(1.25, 12.25) * mm});
            skLineSegment(sketch, "E3.0.11.17", {"start": v(3.75, 11.75) * mm, "end": v(4.25, 11.75) * mm});
            skLineSegment(sketch, "E3.0.11.18", {"start": v(3.75, 12.25) * mm, "end": v(4.25, 12.25) * mm});
            skLineSegment(sketch, "E3.0.11.19", {"start": v(4.75, 11.75) * mm, "end": v(5.25, 11.75) * mm});
            skLineSegment(sketch, "E3.0.11.20", {"start": v(3.25, 11.75) * mm, "end": v(3.25, 12.25) * mm});
            skLineSegment(sketch, "E3.0.11.21", {"start": v(8.75, 11.75) * mm, "end": v(9.25, 11.75) * mm});
            skLineSegment(sketch, "E3.0.11.22", {"start": v(4.75, 12.25) * mm, "end": v(5.25, 12.25) * mm});
            skLineSegment(sketch, "E3.0.11.23", {"start": v(8.75, 12.25) * mm, "end": v(9.25, 12.25) * mm});
            skLineSegment(sketch, "E3.0.11.24", {"start": v(6.75, 11.75) * mm, "end": v(6.75, 12.25) * mm});
            skLineSegment(sketch, "E3.0.11.25", {"start": v(2.75, 11.75) * mm, "end": v(2.75, 12.25) * mm});
            skLineSegment(sketch, "E3.0.11.26", {"start": v(0.75, 11.75) * mm, "end": v(1.75, 11.75) * mm, "construction": true});
            skLineSegment(sketch, "E3.0.11.27", {"start": v(6.25, 11.75) * mm, "end": v(6.25, 12.25) * mm});
            skLineSegment(sketch, "E3.0.11.28", {"start": v(6.75, 12.25) * mm, "end": v(7.25, 12.25) * mm});
            skLineSegment(sketch, "E3.0.11.29", {"start": v(2.25, 11.75) * mm, "end": v(2.25, 12.25) * mm});
            skLineSegment(sketch, "E3.0.11.30", {"start": v(8.25, 11.75) * mm, "end": v(8.25, 12.25) * mm});
            skLineSegment(sketch, "E3.0.11.31", {"start": v(1.75, 11.75) * mm, "end": v(2.25, 11.75) * mm});
            skLineSegment(sketch, "E3.0.11.32", {"start": v(9.25, 11.75) * mm, "end": v(9.25, 12.25) * mm});
            skLineSegment(sketch, "E3.0.11.33", {"start": v(7.75, 11.75) * mm, "end": v(8.25, 11.75) * mm});
            skLineSegment(sketch, "E3.0.11.34", {"start": v(5.75, 11.75) * mm, "end": v(6.25, 11.75) * mm});
            skLineSegment(sketch, "E3.0.11.35", {"start": v(4.75, 11.75) * mm, "end": v(4.75, 12.25) * mm});
            skLineSegment(sketch, "E3.0.11.36", {"start": v(0.75, 11.75) * mm, "end": v(1.25, 11.75) * mm});
            skLineSegment(sketch, "E3.0.12.0", {"start": v(2.75, 13.25) * mm, "end": v(3.25, 13.25) * mm});
            skLineSegment(sketch, "E3.0.12.1", {"start": v(1.25, 12.75) * mm, "end": v(1.25, 13.25) * mm});
            skLineSegment(sketch, "E3.0.12.2", {"start": v(1.75, 13.25) * mm, "end": v(2.25, 13.25) * mm});
            skLineSegment(sketch, "E3.0.12.3", {"start": v(0.75, 12.75) * mm, "end": v(0.75, 13.25) * mm});
            skLineSegment(sketch, "E3.0.12.4", {"start": v(5.75, 13.25) * mm, "end": v(6.25, 13.25) * mm});
            skLineSegment(sketch, "E3.0.12.5", {"start": v(5.25, 12.75) * mm, "end": v(5.25, 13.25) * mm});
            skLineSegment(sketch, "E3.0.12.6", {"start": v(7.75, 12.75) * mm, "end": v(7.75, 13.25) * mm});
            skLineSegment(sketch, "E3.0.12.7", {"start": v(6.75, 12.75) * mm, "end": v(7.25, 12.75) * mm});
            skLineSegment(sketch, "E3.0.12.8", {"start": v(2.75, 12.75) * mm, "end": v(3.25, 12.75) * mm});
            skLineSegment(sketch, "E3.0.12.9", {"start": v(1.75, 12.75) * mm, "end": v(1.75, 13.25) * mm});
            skLineSegment(sketch, "E3.0.12.10", {"start": v(8.75, 12.75) * mm, "end": v(8.75, 13.25) * mm});
            skLineSegment(sketch, "E3.0.12.11", {"start": v(5.75, 12.75) * mm, "end": v(5.75, 13.25) * mm});
            skLineSegment(sketch, "E3.0.12.12", {"start": v(7.25, 12.75) * mm, "end": v(7.25, 13.25) * mm});
            skLineSegment(sketch, "E3.0.12.13", {"start": v(4.25, 12.75) * mm, "end": v(4.25, 13.25) * mm});
            skLineSegment(sketch, "E3.0.12.14", {"start": v(7.75, 13.25) * mm, "end": v(8.25, 13.25) * mm});
            skLineSegment(sketch, "E3.0.12.15", {"start": v(3.75, 12.75) * mm, "end": v(3.75, 13.25) * mm});
            skLineSegment(sketch, "E3.0.12.16", {"start": v(0.75, 13.25) * mm, "end": v(1.25, 13.25) * mm});
            skLineSegment(sketch, "E3.0.12.17", {"start": v(3.75, 12.75) * mm, "end": v(4.25, 12.75) * mm});
            skLineSegment(sketch, "E3.0.12.18", {"start": v(3.75, 13.25) * mm, "end": v(4.25, 13.25) * mm});
            skLineSegment(sketch, "E3.0.12.19", {"start": v(4.75, 12.75) * mm, "end": v(5.25, 12.75) * mm});
            skLineSegment(sketch, "E3.0.12.20", {"start": v(3.25, 12.75) * mm, "end": v(3.25, 13.25) * mm});
            skLineSegment(sketch, "E3.0.12.21", {"start": v(8.75, 12.75) * mm, "end": v(9.25, 12.75) * mm});
            skLineSegment(sketch, "E3.0.12.22", {"start": v(4.75, 13.25) * mm, "end": v(5.25, 13.25) * mm});
            skLineSegment(sketch, "E3.0.12.23", {"start": v(8.75, 13.25) * mm, "end": v(9.25, 13.25) * mm});
            skLineSegment(sketch, "E3.0.12.24", {"start": v(6.75, 12.75) * mm, "end": v(6.75, 13.25) * mm});
            skLineSegment(sketch, "E3.0.12.25", {"start": v(2.75, 12.75) * mm, "end": v(2.75, 13.25) * mm});
            skLineSegment(sketch, "E3.0.12.26", {"start": v(0.75, 12.75) * mm, "end": v(1.75, 12.75) * mm, "construction": true});
            skLineSegment(sketch, "E3.0.12.27", {"start": v(6.25, 12.75) * mm, "end": v(6.25, 13.25) * mm});
            skLineSegment(sketch, "E3.0.12.28", {"start": v(6.75, 13.25) * mm, "end": v(7.25, 13.25) * mm});
            skLineSegment(sketch, "E3.0.12.29", {"start": v(2.25, 12.75) * mm, "end": v(2.25, 13.25) * mm});
            skLineSegment(sketch, "E3.0.12.30", {"start": v(8.25, 12.75) * mm, "end": v(8.25, 13.25) * mm});
            skLineSegment(sketch, "E3.0.12.31", {"start": v(1.75, 12.75) * mm, "end": v(2.25, 12.75) * mm});
            skLineSegment(sketch, "E3.0.12.32", {"start": v(9.25, 12.75) * mm, "end": v(9.25, 13.25) * mm});
            skLineSegment(sketch, "E3.0.12.33", {"start": v(7.75, 12.75) * mm, "end": v(8.25, 12.75) * mm});
            skLineSegment(sketch, "E3.0.12.34", {"start": v(5.75, 12.75) * mm, "end": v(6.25, 12.75) * mm});
            skLineSegment(sketch, "E3.0.12.35", {"start": v(4.75, 12.75) * mm, "end": v(4.75, 13.25) * mm});
            skLineSegment(sketch, "E3.0.12.36", {"start": v(0.75, 12.75) * mm, "end": v(1.25, 12.75) * mm});
            skLineSegment(sketch, "E3.0.13.0", {"start": v(2.75, 14.25) * mm, "end": v(3.25, 14.25) * mm});
            skLineSegment(sketch, "E3.0.13.1", {"start": v(1.25, 13.75) * mm, "end": v(1.25, 14.25) * mm});
            skLineSegment(sketch, "E3.0.13.2", {"start": v(1.75, 14.25) * mm, "end": v(2.25, 14.25) * mm});
            skLineSegment(sketch, "E3.0.13.3", {"start": v(0.75, 13.75) * mm, "end": v(0.75, 14.25) * mm});
            skLineSegment(sketch, "E3.0.13.4", {"start": v(5.75, 14.25) * mm, "end": v(6.25, 14.25) * mm});
            skLineSegment(sketch, "E3.0.13.5", {"start": v(5.25, 13.75) * mm, "end": v(5.25, 14.25) * mm});
            skLineSegment(sketch, "E3.0.13.6", {"start": v(7.75, 13.75) * mm, "end": v(7.75, 14.25) * mm});
            skLineSegment(sketch, "E3.0.13.7", {"start": v(6.75, 13.75) * mm, "end": v(7.25, 13.75) * mm});
            skLineSegment(sketch, "E3.0.13.8", {"start": v(2.75, 13.75) * mm, "end": v(3.25, 13.75) * mm});
            skLineSegment(sketch, "E3.0.13.9", {"start": v(1.75, 13.75) * mm, "end": v(1.75, 14.25) * mm});
            skLineSegment(sketch, "E3.0.13.10", {"start": v(8.75, 13.75) * mm, "end": v(8.75, 14.25) * mm});
            skLineSegment(sketch, "E3.0.13.11", {"start": v(5.75, 13.75) * mm, "end": v(5.75, 14.25) * mm});
            skLineSegment(sketch, "E3.0.13.12", {"start": v(7.25, 13.75) * mm, "end": v(7.25, 14.25) * mm});
            skLineSegment(sketch, "E3.0.13.13", {"start": v(4.25, 13.75) * mm, "end": v(4.25, 14.25) * mm});
            skLineSegment(sketch, "E3.0.13.14", {"start": v(7.75, 14.25) * mm, "end": v(8.25, 14.25) * mm});
            skLineSegment(sketch, "E3.0.13.15", {"start": v(3.75, 13.75) * mm, "end": v(3.75, 14.25) * mm});
            skLineSegment(sketch, "E3.0.13.16", {"start": v(0.75, 14.25) * mm, "end": v(1.25, 14.25) * mm});
            skLineSegment(sketch, "E3.0.13.17", {"start": v(3.75, 13.75) * mm, "end": v(4.25, 13.75) * mm});
            skLineSegment(sketch, "E3.0.13.18", {"start": v(3.75, 14.25) * mm, "end": v(4.25, 14.25) * mm});
            skLineSegment(sketch, "E3.0.13.19", {"start": v(4.75, 13.75) * mm, "end": v(5.25, 13.75) * mm});
            skLineSegment(sketch, "E3.0.13.20", {"start": v(3.25, 13.75) * mm, "end": v(3.25, 14.25) * mm});
            skLineSegment(sketch, "E3.0.13.21", {"start": v(8.75, 13.75) * mm, "end": v(9.25, 13.75) * mm});
            skLineSegment(sketch, "E3.0.13.22", {"start": v(4.75, 14.25) * mm, "end": v(5.25, 14.25) * mm});
            skLineSegment(sketch, "E3.0.13.23", {"start": v(8.75, 14.25) * mm, "end": v(9.25, 14.25) * mm});
            skLineSegment(sketch, "E3.0.13.24", {"start": v(6.75, 13.75) * mm, "end": v(6.75, 14.25) * mm});
            skLineSegment(sketch, "E3.0.13.25", {"start": v(2.75, 13.75) * mm, "end": v(2.75, 14.25) * mm});
            skLineSegment(sketch, "E3.0.13.26", {"start": v(0.75, 13.75) * mm, "end": v(1.75, 13.75) * mm, "construction": true});
            skLineSegment(sketch, "E3.0.13.27", {"start": v(6.25, 13.75) * mm, "end": v(6.25, 14.25) * mm});
            skLineSegment(sketch, "E3.0.13.28", {"start": v(6.75, 14.25) * mm, "end": v(7.25, 14.25) * mm});
            skLineSegment(sketch, "E3.0.13.29", {"start": v(2.25, 13.75) * mm, "end": v(2.25, 14.25) * mm});
            skLineSegment(sketch, "E3.0.13.30", {"start": v(8.25, 13.75) * mm, "end": v(8.25, 14.25) * mm});
            skLineSegment(sketch, "E3.0.13.31", {"start": v(1.75, 13.75) * mm, "end": v(2.25, 13.75) * mm});
            skLineSegment(sketch, "E3.0.13.32", {"start": v(9.25, 13.75) * mm, "end": v(9.25, 14.25) * mm});
            skLineSegment(sketch, "E3.0.13.33", {"start": v(7.75, 13.75) * mm, "end": v(8.25, 13.75) * mm});
            skLineSegment(sketch, "E3.0.13.34", {"start": v(5.75, 13.75) * mm, "end": v(6.25, 13.75) * mm});
            skLineSegment(sketch, "E3.0.13.35", {"start": v(4.75, 13.75) * mm, "end": v(4.75, 14.25) * mm});
            skLineSegment(sketch, "E3.0.13.36", {"start": v(0.75, 13.75) * mm, "end": v(1.25, 13.75) * mm});
            skLineSegment(sketch, "E3.0.14.0", {"start": v(2.75, 15.25) * mm, "end": v(3.25, 15.25) * mm});
            skLineSegment(sketch, "E3.0.14.1", {"start": v(1.25, 14.75) * mm, "end": v(1.25, 15.25) * mm});
            skLineSegment(sketch, "E3.0.14.2", {"start": v(1.75, 15.25) * mm, "end": v(2.25, 15.25) * mm});
            skLineSegment(sketch, "E3.0.14.3", {"start": v(0.75, 14.75) * mm, "end": v(0.75, 15.25) * mm});
            skLineSegment(sketch, "E3.0.14.4", {"start": v(5.75, 15.25) * mm, "end": v(6.25, 15.25) * mm});
            skLineSegment(sketch, "E3.0.14.5", {"start": v(5.25, 14.75) * mm, "end": v(5.25, 15.25) * mm});
            skLineSegment(sketch, "E3.0.14.6", {"start": v(7.75, 14.75) * mm, "end": v(7.75, 15.25) * mm});
            skLineSegment(sketch, "E3.0.14.7", {"start": v(6.75, 14.75) * mm, "end": v(7.25, 14.75) * mm});
            skLineSegment(sketch, "E3.0.14.8", {"start": v(2.75, 14.75) * mm, "end": v(3.25, 14.75) * mm});
            skLineSegment(sketch, "E3.0.14.9", {"start": v(1.75, 14.75) * mm, "end": v(1.75, 15.25) * mm});
            skLineSegment(sketch, "E3.0.14.10", {"start": v(8.75, 14.75) * mm, "end": v(8.75, 15.25) * mm});
            skLineSegment(sketch, "E3.0.14.11", {"start": v(5.75, 14.75) * mm, "end": v(5.75, 15.25) * mm});
            skLineSegment(sketch, "E3.0.14.12", {"start": v(7.25, 14.75) * mm, "end": v(7.25, 15.25) * mm});
            skLineSegment(sketch, "E3.0.14.13", {"start": v(4.25, 14.75) * mm, "end": v(4.25, 15.25) * mm});
            skLineSegment(sketch, "E3.0.14.14", {"start": v(7.75, 15.25) * mm, "end": v(8.25, 15.25) * mm});
            skLineSegment(sketch, "E3.0.14.15", {"start": v(3.75, 14.75) * mm, "end": v(3.75, 15.25) * mm});
            skLineSegment(sketch, "E3.0.14.16", {"start": v(0.75, 15.25) * mm, "end": v(1.25, 15.25) * mm});
            skLineSegment(sketch, "E3.0.14.17", {"start": v(3.75, 14.75) * mm, "end": v(4.25, 14.75) * mm});
            skLineSegment(sketch, "E3.0.14.18", {"start": v(3.75, 15.25) * mm, "end": v(4.25, 15.25) * mm});
            skLineSegment(sketch, "E3.0.14.19", {"start": v(4.75, 14.75) * mm, "end": v(5.25, 14.75) * mm});
            skLineSegment(sketch, "E3.0.14.20", {"start": v(3.25, 14.75) * mm, "end": v(3.25, 15.25) * mm});
            skLineSegment(sketch, "E3.0.14.21", {"start": v(8.75, 14.75) * mm, "end": v(9.25, 14.75) * mm});
            skLineSegment(sketch, "E3.0.14.22", {"start": v(4.75, 15.25) * mm, "end": v(5.25, 15.25) * mm});
            skLineSegment(sketch, "E3.0.14.23", {"start": v(8.75, 15.25) * mm, "end": v(9.25, 15.25) * mm});
            skLineSegment(sketch, "E3.0.14.24", {"start": v(6.75, 14.75) * mm, "end": v(6.75, 15.25) * mm});
            skLineSegment(sketch, "E3.0.14.25", {"start": v(2.75, 14.75) * mm, "end": v(2.75, 15.25) * mm});
            skLineSegment(sketch, "E3.0.14.26", {"start": v(0.75, 14.75) * mm, "end": v(1.75, 14.75) * mm, "construction": true});
            skLineSegment(sketch, "E3.0.14.27", {"start": v(6.25, 14.75) * mm, "end": v(6.25, 15.25) * mm});
            skLineSegment(sketch, "E3.0.14.28", {"start": v(6.75, 15.25) * mm, "end": v(7.25, 15.25) * mm});
            skLineSegment(sketch, "E3.0.14.29", {"start": v(2.25, 14.75) * mm, "end": v(2.25, 15.25) * mm});
            skLineSegment(sketch, "E3.0.14.30", {"start": v(8.25, 14.75) * mm, "end": v(8.25, 15.25) * mm});
            skLineSegment(sketch, "E3.0.14.31", {"start": v(1.75, 14.75) * mm, "end": v(2.25, 14.75) * mm});
            skLineSegment(sketch, "E3.0.14.32", {"start": v(9.25, 14.75) * mm, "end": v(9.25, 15.25) * mm});
            skLineSegment(sketch, "E3.0.14.33", {"start": v(7.75, 14.75) * mm, "end": v(8.25, 14.75) * mm});
            skLineSegment(sketch, "E3.0.14.34", {"start": v(5.75, 14.75) * mm, "end": v(6.25, 14.75) * mm});
            skLineSegment(sketch, "E3.0.14.35", {"start": v(4.75, 14.75) * mm, "end": v(4.75, 15.25) * mm});
            skLineSegment(sketch, "E3.0.14.36", {"start": v(0.75, 14.75) * mm, "end": v(1.25, 14.75) * mm});
            skLineSegment(sketch, "E3.0.15.0", {"start": v(2.75, 16.25) * mm, "end": v(3.25, 16.25) * mm});
            skLineSegment(sketch, "E3.0.15.1", {"start": v(1.25, 15.75) * mm, "end": v(1.25, 16.25) * mm});
            skLineSegment(sketch, "E3.0.15.2", {"start": v(1.75, 16.25) * mm, "end": v(2.25, 16.25) * mm});
            skLineSegment(sketch, "E3.0.15.3", {"start": v(0.75, 15.75) * mm, "end": v(0.75, 16.25) * mm});
            skLineSegment(sketch, "E3.0.15.4", {"start": v(5.75, 16.25) * mm, "end": v(6.25, 16.25) * mm});
            skLineSegment(sketch, "E3.0.15.5", {"start": v(5.25, 15.75) * mm, "end": v(5.25, 16.25) * mm});
            skLineSegment(sketch, "E3.0.15.6", {"start": v(7.75, 15.75) * mm, "end": v(7.75, 16.25) * mm});
            skLineSegment(sketch, "E3.0.15.7", {"start": v(6.75, 15.75) * mm, "end": v(7.25, 15.75) * mm});
            skLineSegment(sketch, "E3.0.15.8", {"start": v(2.75, 15.75) * mm, "end": v(3.25, 15.75) * mm});
            skLineSegment(sketch, "E3.0.15.9", {"start": v(1.75, 15.75) * mm, "end": v(1.75, 16.25) * mm});
            skLineSegment(sketch, "E3.0.15.10", {"start": v(8.75, 15.75) * mm, "end": v(8.75, 16.25) * mm});
            skLineSegment(sketch, "E3.0.15.11", {"start": v(5.75, 15.75) * mm, "end": v(5.75, 16.25) * mm});
            skLineSegment(sketch, "E3.0.15.12", {"start": v(7.25, 15.75) * mm, "end": v(7.25, 16.25) * mm});
            skLineSegment(sketch, "E3.0.15.13", {"start": v(4.25, 15.75) * mm, "end": v(4.25, 16.25) * mm});
            skLineSegment(sketch, "E3.0.15.14", {"start": v(7.75, 16.25) * mm, "end": v(8.25, 16.25) * mm});
            skLineSegment(sketch, "E3.0.15.15", {"start": v(3.75, 15.75) * mm, "end": v(3.75, 16.25) * mm});
            skLineSegment(sketch, "E3.0.15.16", {"start": v(0.75, 16.25) * mm, "end": v(1.25, 16.25) * mm});
            skLineSegment(sketch, "E3.0.15.17", {"start": v(3.75, 15.75) * mm, "end": v(4.25, 15.75) * mm});
            skLineSegment(sketch, "E3.0.15.18", {"start": v(3.75, 16.25) * mm, "end": v(4.25, 16.25) * mm});
            skLineSegment(sketch, "E3.0.15.19", {"start": v(4.75, 15.75) * mm, "end": v(5.25, 15.75) * mm});
            skLineSegment(sketch, "E3.0.15.20", {"start": v(3.25, 15.75) * mm, "end": v(3.25, 16.25) * mm});
            skLineSegment(sketch, "E3.0.15.21", {"start": v(8.75, 15.75) * mm, "end": v(9.25, 15.75) * mm});
            skLineSegment(sketch, "E3.0.15.22", {"start": v(4.75, 16.25) * mm, "end": v(5.25, 16.25) * mm});
            skLineSegment(sketch, "E3.0.15.23", {"start": v(8.75, 16.25) * mm, "end": v(9.25, 16.25) * mm});
            skLineSegment(sketch, "E3.0.15.24", {"start": v(6.75, 15.75) * mm, "end": v(6.75, 16.25) * mm});
            skLineSegment(sketch, "E3.0.15.25", {"start": v(2.75, 15.75) * mm, "end": v(2.75, 16.25) * mm});
            skLineSegment(sketch, "E3.0.15.26", {"start": v(0.75, 15.75) * mm, "end": v(1.75, 15.75) * mm, "construction": true});
            skLineSegment(sketch, "E3.0.15.27", {"start": v(6.25, 15.75) * mm, "end": v(6.25, 16.25) * mm});
            skLineSegment(sketch, "E3.0.15.28", {"start": v(6.75, 16.25) * mm, "end": v(7.25, 16.25) * mm});
            skLineSegment(sketch, "E3.0.15.29", {"start": v(2.25, 15.75) * mm, "end": v(2.25, 16.25) * mm});
            skLineSegment(sketch, "E3.0.15.30", {"start": v(8.25, 15.75) * mm, "end": v(8.25, 16.25) * mm});
            skLineSegment(sketch, "E3.0.15.31", {"start": v(1.75, 15.75) * mm, "end": v(2.25, 15.75) * mm});
            skLineSegment(sketch, "E3.0.15.32", {"start": v(9.25, 15.75) * mm, "end": v(9.25, 16.25) * mm});
            skLineSegment(sketch, "E3.0.15.33", {"start": v(7.75, 15.75) * mm, "end": v(8.25, 15.75) * mm});
            skLineSegment(sketch, "E3.0.15.34", {"start": v(5.75, 15.75) * mm, "end": v(6.25, 15.75) * mm});
            skLineSegment(sketch, "E3.0.15.35", {"start": v(4.75, 15.75) * mm, "end": v(4.75, 16.25) * mm});
            skLineSegment(sketch, "E3.0.15.36", {"start": v(0.75, 15.75) * mm, "end": v(1.25, 15.75) * mm});
            skLineSegment(sketch, "E3.0.16.0", {"start": v(2.75, 17.25) * mm, "end": v(3.25, 17.25) * mm});
            skLineSegment(sketch, "E3.0.16.1", {"start": v(1.25, 16.75) * mm, "end": v(1.25, 17.25) * mm});
            skLineSegment(sketch, "E3.0.16.2", {"start": v(1.75, 17.25) * mm, "end": v(2.25, 17.25) * mm});
            skLineSegment(sketch, "E3.0.16.3", {"start": v(0.75, 16.75) * mm, "end": v(0.75, 17.25) * mm});
            skLineSegment(sketch, "E3.0.16.4", {"start": v(5.75, 17.25) * mm, "end": v(6.25, 17.25) * mm});
            skLineSegment(sketch, "E3.0.16.5", {"start": v(5.25, 16.75) * mm, "end": v(5.25, 17.25) * mm});
            skLineSegment(sketch, "E3.0.16.6", {"start": v(7.75, 16.75) * mm, "end": v(7.75, 17.25) * mm});
            skLineSegment(sketch, "E3.0.16.7", {"start": v(6.75, 16.75) * mm, "end": v(7.25, 16.75) * mm});
            skLineSegment(sketch, "E3.0.16.8", {"start": v(2.75, 16.75) * mm, "end": v(3.25, 16.75) * mm});
            skLineSegment(sketch, "E3.0.16.9", {"start": v(1.75, 16.75) * mm, "end": v(1.75, 17.25) * mm});
            skLineSegment(sketch, "E3.0.16.10", {"start": v(8.75, 16.75) * mm, "end": v(8.75, 17.25) * mm});
            skLineSegment(sketch, "E3.0.16.11", {"start": v(5.75, 16.75) * mm, "end": v(5.75, 17.25) * mm});
            skLineSegment(sketch, "E3.0.16.12", {"start": v(7.25, 16.75) * mm, "end": v(7.25, 17.25) * mm});
            skLineSegment(sketch, "E3.0.16.13", {"start": v(4.25, 16.75) * mm, "end": v(4.25, 17.25) * mm});
            skLineSegment(sketch, "E3.0.16.14", {"start": v(7.75, 17.25) * mm, "end": v(8.25, 17.25) * mm});
            skLineSegment(sketch, "E3.0.16.15", {"start": v(3.75, 16.75) * mm, "end": v(3.75, 17.25) * mm});
            skLineSegment(sketch, "E3.0.16.16", {"start": v(0.75, 17.25) * mm, "end": v(1.25, 17.25) * mm});
            skLineSegment(sketch, "E3.0.16.17", {"start": v(3.75, 16.75) * mm, "end": v(4.25, 16.75) * mm});
            skLineSegment(sketch, "E3.0.16.18", {"start": v(3.75, 17.25) * mm, "end": v(4.25, 17.25) * mm});
            skLineSegment(sketch, "E3.0.16.19", {"start": v(4.75, 16.75) * mm, "end": v(5.25, 16.75) * mm});
            skLineSegment(sketch, "E3.0.16.20", {"start": v(3.25, 16.75) * mm, "end": v(3.25, 17.25) * mm});
            skLineSegment(sketch, "E3.0.16.21", {"start": v(8.75, 16.75) * mm, "end": v(9.25, 16.75) * mm});
            skLineSegment(sketch, "E3.0.16.22", {"start": v(4.75, 17.25) * mm, "end": v(5.25, 17.25) * mm});
            skLineSegment(sketch, "E3.0.16.23", {"start": v(8.75, 17.25) * mm, "end": v(9.25, 17.25) * mm});
            skLineSegment(sketch, "E3.0.16.24", {"start": v(6.75, 16.75) * mm, "end": v(6.75, 17.25) * mm});
            skLineSegment(sketch, "E3.0.16.25", {"start": v(2.75, 16.75) * mm, "end": v(2.75, 17.25) * mm});
            skLineSegment(sketch, "E3.0.16.26", {"start": v(0.75, 16.75) * mm, "end": v(1.75, 16.75) * mm, "construction": true});
            skLineSegment(sketch, "E3.0.16.27", {"start": v(6.25, 16.75) * mm, "end": v(6.25, 17.25) * mm});
            skLineSegment(sketch, "E3.0.16.28", {"start": v(6.75, 17.25) * mm, "end": v(7.25, 17.25) * mm});
            skLineSegment(sketch, "E3.0.16.29", {"start": v(2.25, 16.75) * mm, "end": v(2.25, 17.25) * mm});
            skLineSegment(sketch, "E3.0.16.30", {"start": v(8.25, 16.75) * mm, "end": v(8.25, 17.25) * mm});
            skLineSegment(sketch, "E3.0.16.31", {"start": v(1.75, 16.75) * mm, "end": v(2.25, 16.75) * mm});
            skLineSegment(sketch, "E3.0.16.32", {"start": v(9.25, 16.75) * mm, "end": v(9.25, 17.25) * mm});
            skLineSegment(sketch, "E3.0.16.33", {"start": v(7.75, 16.75) * mm, "end": v(8.25, 16.75) * mm});
            skLineSegment(sketch, "E3.0.16.34", {"start": v(5.75, 16.75) * mm, "end": v(6.25, 16.75) * mm});
            skLineSegment(sketch, "E3.0.16.35", {"start": v(4.75, 16.75) * mm, "end": v(4.75, 17.25) * mm});
            skLineSegment(sketch, "E3.0.16.36", {"start": v(0.75, 16.75) * mm, "end": v(1.25, 16.75) * mm});
            skLineSegment(sketch, "E3.0.17.0", {"start": v(2.75, 18.25) * mm, "end": v(3.25, 18.25) * mm});
            skLineSegment(sketch, "E3.0.17.1", {"start": v(1.25, 17.75) * mm, "end": v(1.25, 18.25) * mm});
            skLineSegment(sketch, "E3.0.17.2", {"start": v(1.75, 18.25) * mm, "end": v(2.25, 18.25) * mm});
            skLineSegment(sketch, "E3.0.17.3", {"start": v(0.75, 17.75) * mm, "end": v(0.75, 18.25) * mm});
            skLineSegment(sketch, "E3.0.17.4", {"start": v(5.75, 18.25) * mm, "end": v(6.25, 18.25) * mm});
            skLineSegment(sketch, "E3.0.17.5", {"start": v(5.25, 17.75) * mm, "end": v(5.25, 18.25) * mm});
            skLineSegment(sketch, "E3.0.17.6", {"start": v(7.75, 17.75) * mm, "end": v(7.75, 18.25) * mm});
            skLineSegment(sketch, "E3.0.17.7", {"start": v(6.75, 17.75) * mm, "end": v(7.25, 17.75) * mm});
            skLineSegment(sketch, "E3.0.17.8", {"start": v(2.75, 17.75) * mm, "end": v(3.25, 17.75) * mm});
            skLineSegment(sketch, "E3.0.17.9", {"start": v(1.75, 17.75) * mm, "end": v(1.75, 18.25) * mm});
            skLineSegment(sketch, "E3.0.17.10", {"start": v(8.75, 17.75) * mm, "end": v(8.75, 18.25) * mm});
            skLineSegment(sketch, "E3.0.17.11", {"start": v(5.75, 17.75) * mm, "end": v(5.75, 18.25) * mm});
            skLineSegment(sketch, "E3.0.17.12", {"start": v(7.25, 17.75) * mm, "end": v(7.25, 18.25) * mm});
            skLineSegment(sketch, "E3.0.17.13", {"start": v(4.25, 17.75) * mm, "end": v(4.25, 18.25) * mm});
            skLineSegment(sketch, "E3.0.17.14", {"start": v(7.75, 18.25) * mm, "end": v(8.25, 18.25) * mm});
            skLineSegment(sketch, "E3.0.17.15", {"start": v(3.75, 17.75) * mm, "end": v(3.75, 18.25) * mm});
            skLineSegment(sketch, "E3.0.17.16", {"start": v(0.75, 18.25) * mm, "end": v(1.25, 18.25) * mm});
            skLineSegment(sketch, "E3.0.17.17", {"start": v(3.75, 17.75) * mm, "end": v(4.25, 17.75) * mm});
            skLineSegment(sketch, "E3.0.17.18", {"start": v(3.75, 18.25) * mm, "end": v(4.25, 18.25) * mm});
            skLineSegment(sketch, "E3.0.17.19", {"start": v(4.75, 17.75) * mm, "end": v(5.25, 17.75) * mm});
            skLineSegment(sketch, "E3.0.17.20", {"start": v(3.25, 17.75) * mm, "end": v(3.25, 18.25) * mm});
            skLineSegment(sketch, "E3.0.17.21", {"start": v(8.75, 17.75) * mm, "end": v(9.25, 17.75) * mm});
            skLineSegment(sketch, "E3.0.17.22", {"start": v(4.75, 18.25) * mm, "end": v(5.25, 18.25) * mm});
            skLineSegment(sketch, "E3.0.17.23", {"start": v(8.75, 18.25) * mm, "end": v(9.25, 18.25) * mm});
            skLineSegment(sketch, "E3.0.17.24", {"start": v(6.75, 17.75) * mm, "end": v(6.75, 18.25) * mm});
            skLineSegment(sketch, "E3.0.17.25", {"start": v(2.75, 17.75) * mm, "end": v(2.75, 18.25) * mm});
            skLineSegment(sketch, "E3.0.17.26", {"start": v(0.75, 17.75) * mm, "end": v(1.75, 17.75) * mm, "construction": true});
            skLineSegment(sketch, "E3.0.17.27", {"start": v(6.25, 17.75) * mm, "end": v(6.25, 18.25) * mm});
            skLineSegment(sketch, "E3.0.17.28", {"start": v(6.75, 18.25) * mm, "end": v(7.25, 18.25) * mm});
            skLineSegment(sketch, "E3.0.17.29", {"start": v(2.25, 17.75) * mm, "end": v(2.25, 18.25) * mm});
            skLineSegment(sketch, "E3.0.17.30", {"start": v(8.25, 17.75) * mm, "end": v(8.25, 18.25) * mm});
            skLineSegment(sketch, "E3.0.17.31", {"start": v(1.75, 17.75) * mm, "end": v(2.25, 17.75) * mm});
            skLineSegment(sketch, "E3.0.17.32", {"start": v(9.25, 17.75) * mm, "end": v(9.25, 18.25) * mm});
            skLineSegment(sketch, "E3.0.17.33", {"start": v(7.75, 17.75) * mm, "end": v(8.25, 17.75) * mm});
            skLineSegment(sketch, "E3.0.17.34", {"start": v(5.75, 17.75) * mm, "end": v(6.25, 17.75) * mm});
            skLineSegment(sketch, "E3.0.17.35", {"start": v(4.75, 17.75) * mm, "end": v(4.75, 18.25) * mm});
            skLineSegment(sketch, "E3.0.17.36", {"start": v(0.75, 17.75) * mm, "end": v(1.25, 17.75) * mm});
            skLineSegment(sketch, "E3.0.18.0", {"start": v(2.75, 19.25) * mm, "end": v(3.25, 19.25) * mm});
            skLineSegment(sketch, "E3.0.18.1", {"start": v(1.25, 18.75) * mm, "end": v(1.25, 19.25) * mm});
            skLineSegment(sketch, "E3.0.18.2", {"start": v(1.75, 19.25) * mm, "end": v(2.25, 19.25) * mm});
            skLineSegment(sketch, "E3.0.18.3", {"start": v(0.75, 18.75) * mm, "end": v(0.75, 19.25) * mm});
            skLineSegment(sketch, "E3.0.18.4", {"start": v(5.75, 19.25) * mm, "end": v(6.25, 19.25) * mm});
            skLineSegment(sketch, "E3.0.18.5", {"start": v(5.25, 18.75) * mm, "end": v(5.25, 19.25) * mm});
            skLineSegment(sketch, "E3.0.18.6", {"start": v(7.75, 18.75) * mm, "end": v(7.75, 19.25) * mm});
            skLineSegment(sketch, "E3.0.18.7", {"start": v(6.75, 18.75) * mm, "end": v(7.25, 18.75) * mm});
            skLineSegment(sketch, "E3.0.18.8", {"start": v(2.75, 18.75) * mm, "end": v(3.25, 18.75) * mm});
            skLineSegment(sketch, "E3.0.18.9", {"start": v(1.75, 18.75) * mm, "end": v(1.75, 19.25) * mm});
            skLineSegment(sketch, "E3.0.18.10", {"start": v(8.75, 18.75) * mm, "end": v(8.75, 19.25) * mm});
            skLineSegment(sketch, "E3.0.18.11", {"start": v(5.75, 18.75) * mm, "end": v(5.75, 19.25) * mm});
            skLineSegment(sketch, "E3.0.18.12", {"start": v(7.25, 18.75) * mm, "end": v(7.25, 19.25) * mm});
            skLineSegment(sketch, "E3.0.18.13", {"start": v(4.25, 18.75) * mm, "end": v(4.25, 19.25) * mm});
            skLineSegment(sketch, "E3.0.18.14", {"start": v(7.75, 19.25) * mm, "end": v(8.25, 19.25) * mm});
            skLineSegment(sketch, "E3.0.18.15", {"start": v(3.75, 18.75) * mm, "end": v(3.75, 19.25) * mm});
            skLineSegment(sketch, "E3.0.18.16", {"start": v(0.75, 19.25) * mm, "end": v(1.25, 19.25) * mm});
            skLineSegment(sketch, "E3.0.18.17", {"start": v(3.75, 18.75) * mm, "end": v(4.25, 18.75) * mm});
            skLineSegment(sketch, "E3.0.18.18", {"start": v(3.75, 19.25) * mm, "end": v(4.25, 19.25) * mm});
            skLineSegment(sketch, "E3.0.18.19", {"start": v(4.75, 18.75) * mm, "end": v(5.25, 18.75) * mm});
            skLineSegment(sketch, "E3.0.18.20", {"start": v(3.25, 18.75) * mm, "end": v(3.25, 19.25) * mm});
            skLineSegment(sketch, "E3.0.18.21", {"start": v(8.75, 18.75) * mm, "end": v(9.25, 18.75) * mm});
            skLineSegment(sketch, "E3.0.18.22", {"start": v(4.75, 19.25) * mm, "end": v(5.25, 19.25) * mm});
            skLineSegment(sketch, "E3.0.18.23", {"start": v(8.75, 19.25) * mm, "end": v(9.25, 19.25) * mm});
            skLineSegment(sketch, "E3.0.18.24", {"start": v(6.75, 18.75) * mm, "end": v(6.75, 19.25) * mm});
            skLineSegment(sketch, "E3.0.18.25", {"start": v(2.75, 18.75) * mm, "end": v(2.75, 19.25) * mm});
            skLineSegment(sketch, "E3.0.18.26", {"start": v(0.75, 18.75) * mm, "end": v(1.75, 18.75) * mm, "construction": true});
            skLineSegment(sketch, "E3.0.18.27", {"start": v(6.25, 18.75) * mm, "end": v(6.25, 19.25) * mm});
            skLineSegment(sketch, "E3.0.18.28", {"start": v(6.75, 19.25) * mm, "end": v(7.25, 19.25) * mm});
            skLineSegment(sketch, "E3.0.18.29", {"start": v(2.25, 18.75) * mm, "end": v(2.25, 19.25) * mm});
            skLineSegment(sketch, "E3.0.18.30", {"start": v(8.25, 18.75) * mm, "end": v(8.25, 19.25) * mm});
            skLineSegment(sketch, "E3.0.18.31", {"start": v(1.75, 18.75) * mm, "end": v(2.25, 18.75) * mm});
            skLineSegment(sketch, "E3.0.18.32", {"start": v(9.25, 18.75) * mm, "end": v(9.25, 19.25) * mm});
            skLineSegment(sketch, "E3.0.18.33", {"start": v(7.75, 18.75) * mm, "end": v(8.25, 18.75) * mm});
            skLineSegment(sketch, "E3.0.18.34", {"start": v(5.75, 18.75) * mm, "end": v(6.25, 18.75) * mm});
            skLineSegment(sketch, "E3.0.18.35", {"start": v(4.75, 18.75) * mm, "end": v(4.75, 19.25) * mm});
            skLineSegment(sketch, "E3.0.18.36", {"start": v(0.75, 18.75) * mm, "end": v(1.25, 18.75) * mm});
            skLineSegment(sketch, "E3.0.19.0", {"start": v(2.75, 20.25) * mm, "end": v(3.25, 20.25) * mm});
            skLineSegment(sketch, "E3.0.19.1", {"start": v(1.25, 19.75) * mm, "end": v(1.25, 20.25) * mm});
            skLineSegment(sketch, "E3.0.19.2", {"start": v(1.75, 20.25) * mm, "end": v(2.25, 20.25) * mm});
            skLineSegment(sketch, "E3.0.19.3", {"start": v(0.75, 19.75) * mm, "end": v(0.75, 20.25) * mm});
            skLineSegment(sketch, "E3.0.19.4", {"start": v(5.75, 20.25) * mm, "end": v(6.25, 20.25) * mm});
            skLineSegment(sketch, "E3.0.19.5", {"start": v(5.25, 19.75) * mm, "end": v(5.25, 20.25) * mm});
            skLineSegment(sketch, "E3.0.19.6", {"start": v(7.75, 19.75) * mm, "end": v(7.75, 20.25) * mm});
            skLineSegment(sketch, "E3.0.19.7", {"start": v(6.75, 19.75) * mm, "end": v(7.25, 19.75) * mm});
            skLineSegment(sketch, "E3.0.19.8", {"start": v(2.75, 19.75) * mm, "end": v(3.25, 19.75) * mm});
            skLineSegment(sketch, "E3.0.19.9", {"start": v(1.75, 19.75) * mm, "end": v(1.75, 20.25) * mm});
            skLineSegment(sketch, "E3.0.19.10", {"start": v(8.75, 19.75) * mm, "end": v(8.75, 20.25) * mm});
            skLineSegment(sketch, "E3.0.19.11", {"start": v(5.75, 19.75) * mm, "end": v(5.75, 20.25) * mm});
            skLineSegment(sketch, "E3.0.19.12", {"start": v(7.25, 19.75) * mm, "end": v(7.25, 20.25) * mm});
            skLineSegment(sketch, "E3.0.19.13", {"start": v(4.25, 19.75) * mm, "end": v(4.25, 20.25) * mm});
            skLineSegment(sketch, "E3.0.19.14", {"start": v(7.75, 20.25) * mm, "end": v(8.25, 20.25) * mm});
            skLineSegment(sketch, "E3.0.19.15", {"start": v(3.75, 19.75) * mm, "end": v(3.75, 20.25) * mm});
            skLineSegment(sketch, "E3.0.19.16", {"start": v(0.75, 20.25) * mm, "end": v(1.25, 20.25) * mm});
            skLineSegment(sketch, "E3.0.19.17", {"start": v(3.75, 19.75) * mm, "end": v(4.25, 19.75) * mm});
            skLineSegment(sketch, "E3.0.19.18", {"start": v(3.75, 20.25) * mm, "end": v(4.25, 20.25) * mm});
            skLineSegment(sketch, "E3.0.19.19", {"start": v(4.75, 19.75) * mm, "end": v(5.25, 19.75) * mm});
            skLineSegment(sketch, "E3.0.19.20", {"start": v(3.25, 19.75) * mm, "end": v(3.25, 20.25) * mm});
            skLineSegment(sketch, "E3.0.19.21", {"start": v(8.75, 19.75) * mm, "end": v(9.25, 19.75) * mm});
            skLineSegment(sketch, "E3.0.19.22", {"start": v(4.75, 20.25) * mm, "end": v(5.25, 20.25) * mm});
            skLineSegment(sketch, "E3.0.19.23", {"start": v(8.75, 20.25) * mm, "end": v(9.25, 20.25) * mm});
            skLineSegment(sketch, "E3.0.19.24", {"start": v(6.75, 19.75) * mm, "end": v(6.75, 20.25) * mm});
            skLineSegment(sketch, "E3.0.19.25", {"start": v(2.75, 19.75) * mm, "end": v(2.75, 20.25) * mm});
            skLineSegment(sketch, "E3.0.19.26", {"start": v(0.75, 19.75) * mm, "end": v(1.75, 19.75) * mm, "construction": true});
            skLineSegment(sketch, "E3.0.19.27", {"start": v(6.25, 19.75) * mm, "end": v(6.25, 20.25) * mm});
            skLineSegment(sketch, "E3.0.19.28", {"start": v(6.75, 20.25) * mm, "end": v(7.25, 20.25) * mm});
            skLineSegment(sketch, "E3.0.19.29", {"start": v(2.25, 19.75) * mm, "end": v(2.25, 20.25) * mm});
            skLineSegment(sketch, "E3.0.19.30", {"start": v(8.25, 19.75) * mm, "end": v(8.25, 20.25) * mm});
            skLineSegment(sketch, "E3.0.19.31", {"start": v(1.75, 19.75) * mm, "end": v(2.25, 19.75) * mm});
            skLineSegment(sketch, "E3.0.19.32", {"start": v(9.25, 19.75) * mm, "end": v(9.25, 20.25) * mm});
            skLineSegment(sketch, "E3.0.19.33", {"start": v(7.75, 19.75) * mm, "end": v(8.25, 19.75) * mm});
            skLineSegment(sketch, "E3.0.19.34", {"start": v(5.75, 19.75) * mm, "end": v(6.25, 19.75) * mm});
            skLineSegment(sketch, "E3.0.19.35", {"start": v(4.75, 19.75) * mm, "end": v(4.75, 20.25) * mm});
            skLineSegment(sketch, "E3.0.19.36", {"start": v(0.75, 19.75) * mm, "end": v(1.25, 19.75) * mm});
            skLineSegment(sketch, "E3.0.20.0", {"start": v(2.75, 21.25) * mm, "end": v(3.25, 21.25) * mm});
            skLineSegment(sketch, "E3.0.20.1", {"start": v(1.25, 20.75) * mm, "end": v(1.25, 21.25) * mm});
            skLineSegment(sketch, "E3.0.20.2", {"start": v(1.75, 21.25) * mm, "end": v(2.25, 21.25) * mm});
            skLineSegment(sketch, "E3.0.20.3", {"start": v(0.75, 20.75) * mm, "end": v(0.75, 21.25) * mm});
            skLineSegment(sketch, "E3.0.20.4", {"start": v(5.75, 21.25) * mm, "end": v(6.25, 21.25) * mm});
            skLineSegment(sketch, "E3.0.20.5", {"start": v(5.25, 20.75) * mm, "end": v(5.25, 21.25) * mm});
            skLineSegment(sketch, "E3.0.20.6", {"start": v(7.75, 20.75) * mm, "end": v(7.75, 21.25) * mm});
            skLineSegment(sketch, "E3.0.20.7", {"start": v(6.75, 20.75) * mm, "end": v(7.25, 20.75) * mm});
            skLineSegment(sketch, "E3.0.20.8", {"start": v(2.75, 20.75) * mm, "end": v(3.25, 20.75) * mm});
            skLineSegment(sketch, "E3.0.20.9", {"start": v(1.75, 20.75) * mm, "end": v(1.75, 21.25) * mm});
            skLineSegment(sketch, "E3.0.20.10", {"start": v(8.75, 20.75) * mm, "end": v(8.75, 21.25) * mm});
            skLineSegment(sketch, "E3.0.20.11", {"start": v(5.75, 20.75) * mm, "end": v(5.75, 21.25) * mm});
            skLineSegment(sketch, "E3.0.20.12", {"start": v(7.25, 20.75) * mm, "end": v(7.25, 21.25) * mm});
            skLineSegment(sketch, "E3.0.20.13", {"start": v(4.25, 20.75) * mm, "end": v(4.25, 21.25) * mm});
            skLineSegment(sketch, "E3.0.20.14", {"start": v(7.75, 21.25) * mm, "end": v(8.25, 21.25) * mm});
            skLineSegment(sketch, "E3.0.20.15", {"start": v(3.75, 20.75) * mm, "end": v(3.75, 21.25) * mm});
            skLineSegment(sketch, "E3.0.20.16", {"start": v(0.75, 21.25) * mm, "end": v(1.25, 21.25) * mm});
            skLineSegment(sketch, "E3.0.20.17", {"start": v(3.75, 20.75) * mm, "end": v(4.25, 20.75) * mm});
            skLineSegment(sketch, "E3.0.20.18", {"start": v(3.75, 21.25) * mm, "end": v(4.25, 21.25) * mm});
            skLineSegment(sketch, "E3.0.20.19", {"start": v(4.75, 20.75) * mm, "end": v(5.25, 20.75) * mm});
            skLineSegment(sketch, "E3.0.20.20", {"start": v(3.25, 20.75) * mm, "end": v(3.25, 21.25) * mm});
            skLineSegment(sketch, "E3.0.20.21", {"start": v(8.75, 20.75) * mm, "end": v(9.25, 20.75) * mm});
            skLineSegment(sketch, "E3.0.20.22", {"start": v(4.75, 21.25) * mm, "end": v(5.25, 21.25) * mm});
            skLineSegment(sketch, "E3.0.20.23", {"start": v(8.75, 21.25) * mm, "end": v(9.25, 21.25) * mm});
            skLineSegment(sketch, "E3.0.20.24", {"start": v(6.75, 20.75) * mm, "end": v(6.75, 21.25) * mm});
            skLineSegment(sketch, "E3.0.20.25", {"start": v(2.75, 20.75) * mm, "end": v(2.75, 21.25) * mm});
            skLineSegment(sketch, "E3.0.20.26", {"start": v(0.75, 20.75) * mm, "end": v(1.75, 20.75) * mm, "construction": true});
            skLineSegment(sketch, "E3.0.20.27", {"start": v(6.25, 20.75) * mm, "end": v(6.25, 21.25) * mm});
            skLineSegment(sketch, "E3.0.20.28", {"start": v(6.75, 21.25) * mm, "end": v(7.25, 21.25) * mm});
            skLineSegment(sketch, "E3.0.20.29", {"start": v(2.25, 20.75) * mm, "end": v(2.25, 21.25) * mm});
            skLineSegment(sketch, "E3.0.20.30", {"start": v(8.25, 20.75) * mm, "end": v(8.25, 21.25) * mm});
            skLineSegment(sketch, "E3.0.20.31", {"start": v(1.75, 20.75) * mm, "end": v(2.25, 20.75) * mm});
            skLineSegment(sketch, "E3.0.20.32", {"start": v(9.25, 20.75) * mm, "end": v(9.25, 21.25) * mm});
            skLineSegment(sketch, "E3.0.20.33", {"start": v(7.75, 20.75) * mm, "end": v(8.25, 20.75) * mm});
            skLineSegment(sketch, "E3.0.20.34", {"start": v(5.75, 20.75) * mm, "end": v(6.25, 20.75) * mm});
            skLineSegment(sketch, "E3.0.20.35", {"start": v(4.75, 20.75) * mm, "end": v(4.75, 21.25) * mm});
            skLineSegment(sketch, "E3.0.20.36", {"start": v(0.75, 20.75) * mm, "end": v(1.25, 20.75) * mm});
            skLineSegment(sketch, "E3.0.21.0", {"start": v(2.75, 22.25) * mm, "end": v(3.25, 22.25) * mm});
            skLineSegment(sketch, "E3.0.21.1", {"start": v(1.25, 21.75) * mm, "end": v(1.25, 22.25) * mm});
            skLineSegment(sketch, "E3.0.21.2", {"start": v(1.75, 22.25) * mm, "end": v(2.25, 22.25) * mm});
            skLineSegment(sketch, "E3.0.21.3", {"start": v(0.75, 21.75) * mm, "end": v(0.75, 22.25) * mm});
            skLineSegment(sketch, "E3.0.21.4", {"start": v(5.75, 22.25) * mm, "end": v(6.25, 22.25) * mm});
            skLineSegment(sketch, "E3.0.21.5", {"start": v(5.25, 21.75) * mm, "end": v(5.25, 22.25) * mm});
            skLineSegment(sketch, "E3.0.21.6", {"start": v(7.75, 21.75) * mm, "end": v(7.75, 22.25) * mm});
            skLineSegment(sketch, "E3.0.21.7", {"start": v(6.75, 21.75) * mm, "end": v(7.25, 21.75) * mm});
            skLineSegment(sketch, "E3.0.21.8", {"start": v(2.75, 21.75) * mm, "end": v(3.25, 21.75) * mm});
            skLineSegment(sketch, "E3.0.21.9", {"start": v(1.75, 21.75) * mm, "end": v(1.75, 22.25) * mm});
            skLineSegment(sketch, "E3.0.21.10", {"start": v(8.75, 21.75) * mm, "end": v(8.75, 22.25) * mm});
            skLineSegment(sketch, "E3.0.21.11", {"start": v(5.75, 21.75) * mm, "end": v(5.75, 22.25) * mm});
            skLineSegment(sketch, "E3.0.21.12", {"start": v(7.25, 21.75) * mm, "end": v(7.25, 22.25) * mm});
            skLineSegment(sketch, "E3.0.21.13", {"start": v(4.25, 21.75) * mm, "end": v(4.25, 22.25) * mm});
            skLineSegment(sketch, "E3.0.21.14", {"start": v(7.75, 22.25) * mm, "end": v(8.25, 22.25) * mm});
            skLineSegment(sketch, "E3.0.21.15", {"start": v(3.75, 21.75) * mm, "end": v(3.75, 22.25) * mm});
            skLineSegment(sketch, "E3.0.21.16", {"start": v(0.75, 22.25) * mm, "end": v(1.25, 22.25) * mm});
            skLineSegment(sketch, "E3.0.21.17", {"start": v(3.75, 21.75) * mm, "end": v(4.25, 21.75) * mm});
            skLineSegment(sketch, "E3.0.21.18", {"start": v(3.75, 22.25) * mm, "end": v(4.25, 22.25) * mm});
            skLineSegment(sketch, "E3.0.21.19", {"start": v(4.75, 21.75) * mm, "end": v(5.25, 21.75) * mm});
            skLineSegment(sketch, "E3.0.21.20", {"start": v(3.25, 21.75) * mm, "end": v(3.25, 22.25) * mm});
            skLineSegment(sketch, "E3.0.21.21", {"start": v(8.75, 21.75) * mm, "end": v(9.25, 21.75) * mm});
            skLineSegment(sketch, "E3.0.21.22", {"start": v(4.75, 22.25) * mm, "end": v(5.25, 22.25) * mm});
            skLineSegment(sketch, "E3.0.21.23", {"start": v(8.75, 22.25) * mm, "end": v(9.25, 22.25) * mm});
            skLineSegment(sketch, "E3.0.21.24", {"start": v(6.75, 21.75) * mm, "end": v(6.75, 22.25) * mm});
            skLineSegment(sketch, "E3.0.21.25", {"start": v(2.75, 21.75) * mm, "end": v(2.75, 22.25) * mm});
            skLineSegment(sketch, "E3.0.21.26", {"start": v(0.75, 21.75) * mm, "end": v(1.75, 21.75) * mm, "construction": true});
            skLineSegment(sketch, "E3.0.21.27", {"start": v(6.25, 21.75) * mm, "end": v(6.25, 22.25) * mm});
            skLineSegment(sketch, "E3.0.21.28", {"start": v(6.75, 22.25) * mm, "end": v(7.25, 22.25) * mm});
            skLineSegment(sketch, "E3.0.21.29", {"start": v(2.25, 21.75) * mm, "end": v(2.25, 22.25) * mm});
            skLineSegment(sketch, "E3.0.21.30", {"start": v(8.25, 21.75) * mm, "end": v(8.25, 22.25) * mm});
            skLineSegment(sketch, "E3.0.21.31", {"start": v(1.75, 21.75) * mm, "end": v(2.25, 21.75) * mm});
            skLineSegment(sketch, "E3.0.21.32", {"start": v(9.25, 21.75) * mm, "end": v(9.25, 22.25) * mm});
            skLineSegment(sketch, "E3.0.21.33", {"start": v(7.75, 21.75) * mm, "end": v(8.25, 21.75) * mm});
            skLineSegment(sketch, "E3.0.21.34", {"start": v(5.75, 21.75) * mm, "end": v(6.25, 21.75) * mm});
            skLineSegment(sketch, "E3.0.21.35", {"start": v(4.75, 21.75) * mm, "end": v(4.75, 22.25) * mm});
            skLineSegment(sketch, "E3.0.21.36", {"start": v(0.75, 21.75) * mm, "end": v(1.25, 21.75) * mm});
            skLineSegment(sketch, "E3.0.22.0", {"start": v(2.75, 23.25) * mm, "end": v(3.25, 23.25) * mm});
            skLineSegment(sketch, "E3.0.22.1", {"start": v(1.25, 22.75) * mm, "end": v(1.25, 23.25) * mm});
            skLineSegment(sketch, "E3.0.22.2", {"start": v(1.75, 23.25) * mm, "end": v(2.25, 23.25) * mm});
            skLineSegment(sketch, "E3.0.22.3", {"start": v(0.75, 22.75) * mm, "end": v(0.75, 23.25) * mm});
            skLineSegment(sketch, "E3.0.22.4", {"start": v(5.75, 23.25) * mm, "end": v(6.25, 23.25) * mm});
            skLineSegment(sketch, "E3.0.22.5", {"start": v(5.25, 22.75) * mm, "end": v(5.25, 23.25) * mm});
            skLineSegment(sketch, "E3.0.22.6", {"start": v(7.75, 22.75) * mm, "end": v(7.75, 23.25) * mm});
            skLineSegment(sketch, "E3.0.22.7", {"start": v(6.75, 22.75) * mm, "end": v(7.25, 22.75) * mm});
            skLineSegment(sketch, "E3.0.22.8", {"start": v(2.75, 22.75) * mm, "end": v(3.25, 22.75) * mm});
            skLineSegment(sketch, "E3.0.22.9", {"start": v(1.75, 22.75) * mm, "end": v(1.75, 23.25) * mm});
            skLineSegment(sketch, "E3.0.22.10", {"start": v(8.75, 22.75) * mm, "end": v(8.75, 23.25) * mm});
            skLineSegment(sketch, "E3.0.22.11", {"start": v(5.75, 22.75) * mm, "end": v(5.75, 23.25) * mm});
            skLineSegment(sketch, "E3.0.22.12", {"start": v(7.25, 22.75) * mm, "end": v(7.25, 23.25) * mm});
            skLineSegment(sketch, "E3.0.22.13", {"start": v(4.25, 22.75) * mm, "end": v(4.25, 23.25) * mm});
            skLineSegment(sketch, "E3.0.22.14", {"start": v(7.75, 23.25) * mm, "end": v(8.25, 23.25) * mm});
            skLineSegment(sketch, "E3.0.22.15", {"start": v(3.75, 22.75) * mm, "end": v(3.75, 23.25) * mm});
            skLineSegment(sketch, "E3.0.22.16", {"start": v(0.75, 23.25) * mm, "end": v(1.25, 23.25) * mm});
            skLineSegment(sketch, "E3.0.22.17", {"start": v(3.75, 22.75) * mm, "end": v(4.25, 22.75) * mm});
            skLineSegment(sketch, "E3.0.22.18", {"start": v(3.75, 23.25) * mm, "end": v(4.25, 23.25) * mm});
            skLineSegment(sketch, "E3.0.22.19", {"start": v(4.75, 22.75) * mm, "end": v(5.25, 22.75) * mm});
            skLineSegment(sketch, "E3.0.22.20", {"start": v(3.25, 22.75) * mm, "end": v(3.25, 23.25) * mm});
            skLineSegment(sketch, "E3.0.22.21", {"start": v(8.75, 22.75) * mm, "end": v(9.25, 22.75) * mm});
            skLineSegment(sketch, "E3.0.22.22", {"start": v(4.75, 23.25) * mm, "end": v(5.25, 23.25) * mm});
            skLineSegment(sketch, "E3.0.22.23", {"start": v(8.75, 23.25) * mm, "end": v(9.25, 23.25) * mm});
            skLineSegment(sketch, "E3.0.22.24", {"start": v(6.75, 22.75) * mm, "end": v(6.75, 23.25) * mm});
            skLineSegment(sketch, "E3.0.22.25", {"start": v(2.75, 22.75) * mm, "end": v(2.75, 23.25) * mm});
            skLineSegment(sketch, "E3.0.22.26", {"start": v(0.75, 22.75) * mm, "end": v(1.75, 22.75) * mm, "construction": true});
            skLineSegment(sketch, "E3.0.22.27", {"start": v(6.25, 22.75) * mm, "end": v(6.25, 23.25) * mm});
            skLineSegment(sketch, "E3.0.22.28", {"start": v(6.75, 23.25) * mm, "end": v(7.25, 23.25) * mm});
            skLineSegment(sketch, "E3.0.22.29", {"start": v(2.25, 22.75) * mm, "end": v(2.25, 23.25) * mm});
            skLineSegment(sketch, "E3.0.22.30", {"start": v(8.25, 22.75) * mm, "end": v(8.25, 23.25) * mm});
            skLineSegment(sketch, "E3.0.22.31", {"start": v(1.75, 22.75) * mm, "end": v(2.25, 22.75) * mm});
            skLineSegment(sketch, "E3.0.22.32", {"start": v(9.25, 22.75) * mm, "end": v(9.25, 23.25) * mm});
            skLineSegment(sketch, "E3.0.22.33", {"start": v(7.75, 22.75) * mm, "end": v(8.25, 22.75) * mm});
            skLineSegment(sketch, "E3.0.22.34", {"start": v(5.75, 22.75) * mm, "end": v(6.25, 22.75) * mm});
            skLineSegment(sketch, "E3.0.22.35", {"start": v(4.75, 22.75) * mm, "end": v(4.75, 23.25) * mm});
            skLineSegment(sketch, "E3.0.22.36", {"start": v(0.75, 22.75) * mm, "end": v(1.25, 22.75) * mm});
            skLineSegment(sketch, "E3.0.23.0", {"start": v(2.75, 24.25) * mm, "end": v(3.25, 24.25) * mm});
            skLineSegment(sketch, "E3.0.23.1", {"start": v(1.25, 23.75) * mm, "end": v(1.25, 24.25) * mm});
            skLineSegment(sketch, "E3.0.23.2", {"start": v(1.75, 24.25) * mm, "end": v(2.25, 24.25) * mm});
            skLineSegment(sketch, "E3.0.23.3", {"start": v(0.75, 23.75) * mm, "end": v(0.75, 24.25) * mm});
            skLineSegment(sketch, "E3.0.23.4", {"start": v(5.75, 24.25) * mm, "end": v(6.25, 24.25) * mm});
            skLineSegment(sketch, "E3.0.23.5", {"start": v(5.25, 23.75) * mm, "end": v(5.25, 24.25) * mm});
            skLineSegment(sketch, "E3.0.23.6", {"start": v(7.75, 23.75) * mm, "end": v(7.75, 24.25) * mm});
            skLineSegment(sketch, "E3.0.23.7", {"start": v(6.75, 23.75) * mm, "end": v(7.25, 23.75) * mm});
            skLineSegment(sketch, "E3.0.23.8", {"start": v(2.75, 23.75) * mm, "end": v(3.25, 23.75) * mm});
            skLineSegment(sketch, "E3.0.23.9", {"start": v(1.75, 23.75) * mm, "end": v(1.75, 24.25) * mm});
            skLineSegment(sketch, "E3.0.23.10", {"start": v(8.75, 23.75) * mm, "end": v(8.75, 24.25) * mm});
            skLineSegment(sketch, "E3.0.23.11", {"start": v(5.75, 23.75) * mm, "end": v(5.75, 24.25) * mm});
            skLineSegment(sketch, "E3.0.23.12", {"start": v(7.25, 23.75) * mm, "end": v(7.25, 24.25) * mm});
            skLineSegment(sketch, "E3.0.23.13", {"start": v(4.25, 23.75) * mm, "end": v(4.25, 24.25) * mm});
            skLineSegment(sketch, "E3.0.23.14", {"start": v(7.75, 24.25) * mm, "end": v(8.25, 24.25) * mm});
            skLineSegment(sketch, "E3.0.23.15", {"start": v(3.75, 23.75) * mm, "end": v(3.75, 24.25) * mm});
            skLineSegment(sketch, "E3.0.23.16", {"start": v(0.75, 24.25) * mm, "end": v(1.25, 24.25) * mm});
            skLineSegment(sketch, "E3.0.23.17", {"start": v(3.75, 23.75) * mm, "end": v(4.25, 23.75) * mm});
            skLineSegment(sketch, "E3.0.23.18", {"start": v(3.75, 24.25) * mm, "end": v(4.25, 24.25) * mm});
            skLineSegment(sketch, "E3.0.23.19", {"start": v(4.75, 23.75) * mm, "end": v(5.25, 23.75) * mm});
            skLineSegment(sketch, "E3.0.23.20", {"start": v(3.25, 23.75) * mm, "end": v(3.25, 24.25) * mm});
            skLineSegment(sketch, "E3.0.23.21", {"start": v(8.75, 23.75) * mm, "end": v(9.25, 23.75) * mm});
            skLineSegment(sketch, "E3.0.23.22", {"start": v(4.75, 24.25) * mm, "end": v(5.25, 24.25) * mm});
            skLineSegment(sketch, "E3.0.23.23", {"start": v(8.75, 24.25) * mm, "end": v(9.25, 24.25) * mm});
            skLineSegment(sketch, "E3.0.23.24", {"start": v(6.75, 23.75) * mm, "end": v(6.75, 24.25) * mm});
            skLineSegment(sketch, "E3.0.23.25", {"start": v(2.75, 23.75) * mm, "end": v(2.75, 24.25) * mm});
            skLineSegment(sketch, "E3.0.23.26", {"start": v(0.75, 23.75) * mm, "end": v(1.75, 23.75) * mm, "construction": true});
            skLineSegment(sketch, "E3.0.23.27", {"start": v(6.25, 23.75) * mm, "end": v(6.25, 24.25) * mm});
            skLineSegment(sketch, "E3.0.23.28", {"start": v(6.75, 24.25) * mm, "end": v(7.25, 24.25) * mm});
            skLineSegment(sketch, "E3.0.23.29", {"start": v(2.25, 23.75) * mm, "end": v(2.25, 24.25) * mm});
            skLineSegment(sketch, "E3.0.23.30", {"start": v(8.25, 23.75) * mm, "end": v(8.25, 24.25) * mm});
            skLineSegment(sketch, "E3.0.23.31", {"start": v(1.75, 23.75) * mm, "end": v(2.25, 23.75) * mm});
            skLineSegment(sketch, "E3.0.23.32", {"start": v(9.25, 23.75) * mm, "end": v(9.25, 24.25) * mm});
            skLineSegment(sketch, "E3.0.23.33", {"start": v(7.75, 23.75) * mm, "end": v(8.25, 23.75) * mm});
            skLineSegment(sketch, "E3.0.23.34", {"start": v(5.75, 23.75) * mm, "end": v(6.25, 23.75) * mm});
            skLineSegment(sketch, "E3.0.23.35", {"start": v(4.75, 23.75) * mm, "end": v(4.75, 24.25) * mm});
            skLineSegment(sketch, "E3.0.23.36", {"start": v(0.75, 23.75) * mm, "end": v(1.25, 23.75) * mm});
            skLineSegment(sketch, "E3.0.24.0", {"start": v(2.75, 25.25) * mm, "end": v(3.25, 25.25) * mm});
            skLineSegment(sketch, "E3.0.24.1", {"start": v(1.25, 24.75) * mm, "end": v(1.25, 25.25) * mm});
            skLineSegment(sketch, "E3.0.24.2", {"start": v(1.75, 25.25) * mm, "end": v(2.25, 25.25) * mm});
            skLineSegment(sketch, "E3.0.24.3", {"start": v(0.75, 24.75) * mm, "end": v(0.75, 25.25) * mm});
            skLineSegment(sketch, "E3.0.24.4", {"start": v(5.75, 25.25) * mm, "end": v(6.25, 25.25) * mm});
            skLineSegment(sketch, "E3.0.24.5", {"start": v(5.25, 24.75) * mm, "end": v(5.25, 25.25) * mm});
            skLineSegment(sketch, "E3.0.24.6", {"start": v(7.75, 24.75) * mm, "end": v(7.75, 25.25) * mm});
            skLineSegment(sketch, "E3.0.24.7", {"start": v(6.75, 24.75) * mm, "end": v(7.25, 24.75) * mm});
            skLineSegment(sketch, "E3.0.24.8", {"start": v(2.75, 24.75) * mm, "end": v(3.25, 24.75) * mm});
            skLineSegment(sketch, "E3.0.24.9", {"start": v(1.75, 24.75) * mm, "end": v(1.75, 25.25) * mm});
            skLineSegment(sketch, "E3.0.24.10", {"start": v(8.75, 24.75) * mm, "end": v(8.75, 25.25) * mm});
            skLineSegment(sketch, "E3.0.24.11", {"start": v(5.75, 24.75) * mm, "end": v(5.75, 25.25) * mm});
            skLineSegment(sketch, "E3.0.24.12", {"start": v(7.25, 24.75) * mm, "end": v(7.25, 25.25) * mm});
            skLineSegment(sketch, "E3.0.24.13", {"start": v(4.25, 24.75) * mm, "end": v(4.25, 25.25) * mm});
            skLineSegment(sketch, "E3.0.24.14", {"start": v(7.75, 25.25) * mm, "end": v(8.25, 25.25) * mm});
            skLineSegment(sketch, "E3.0.24.15", {"start": v(3.75, 24.75) * mm, "end": v(3.75, 25.25) * mm});
            skLineSegment(sketch, "E3.0.24.16", {"start": v(0.75, 25.25) * mm, "end": v(1.25, 25.25) * mm});
            skLineSegment(sketch, "E3.0.24.17", {"start": v(3.75, 24.75) * mm, "end": v(4.25, 24.75) * mm});
            skLineSegment(sketch, "E3.0.24.18", {"start": v(3.75, 25.25) * mm, "end": v(4.25, 25.25) * mm});
            skLineSegment(sketch, "E3.0.24.19", {"start": v(4.75, 24.75) * mm, "end": v(5.25, 24.75) * mm});
            skLineSegment(sketch, "E3.0.24.20", {"start": v(3.25, 24.75) * mm, "end": v(3.25, 25.25) * mm});
            skLineSegment(sketch, "E3.0.24.21", {"start": v(8.75, 24.75) * mm, "end": v(9.25, 24.75) * mm});
            skLineSegment(sketch, "E3.0.24.22", {"start": v(4.75, 25.25) * mm, "end": v(5.25, 25.25) * mm});
            skLineSegment(sketch, "E3.0.24.23", {"start": v(8.75, 25.25) * mm, "end": v(9.25, 25.25) * mm});
            skLineSegment(sketch, "E3.0.24.24", {"start": v(6.75, 24.75) * mm, "end": v(6.75, 25.25) * mm});
            skLineSegment(sketch, "E3.0.24.25", {"start": v(2.75, 24.75) * mm, "end": v(2.75, 25.25) * mm});
            skLineSegment(sketch, "E3.0.24.26", {"start": v(0.75, 24.75) * mm, "end": v(1.75, 24.75) * mm, "construction": true});
            skLineSegment(sketch, "E3.0.24.27", {"start": v(6.25, 24.75) * mm, "end": v(6.25, 25.25) * mm});
            skLineSegment(sketch, "E3.0.24.28", {"start": v(6.75, 25.25) * mm, "end": v(7.25, 25.25) * mm});
            skLineSegment(sketch, "E3.0.24.29", {"start": v(2.25, 24.75) * mm, "end": v(2.25, 25.25) * mm});
            skLineSegment(sketch, "E3.0.24.30", {"start": v(8.25, 24.75) * mm, "end": v(8.25, 25.25) * mm});
            skLineSegment(sketch, "E3.0.24.31", {"start": v(1.75, 24.75) * mm, "end": v(2.25, 24.75) * mm});
            skLineSegment(sketch, "E3.0.24.32", {"start": v(9.25, 24.75) * mm, "end": v(9.25, 25.25) * mm});
            skLineSegment(sketch, "E3.0.24.33", {"start": v(7.75, 24.75) * mm, "end": v(8.25, 24.75) * mm});
            skLineSegment(sketch, "E3.0.24.34", {"start": v(5.75, 24.75) * mm, "end": v(6.25, 24.75) * mm});
            skLineSegment(sketch, "E3.0.24.35", {"start": v(4.75, 24.75) * mm, "end": v(4.75, 25.25) * mm});
            skLineSegment(sketch, "E3.0.24.36", {"start": v(0.75, 24.75) * mm, "end": v(1.25, 24.75) * mm});
            skLineSegment(sketch, "E3.0.25.0", {"start": v(2.75, 26.25) * mm, "end": v(3.25, 26.25) * mm});
            skLineSegment(sketch, "E3.0.25.1", {"start": v(1.25, 25.75) * mm, "end": v(1.25, 26.25) * mm});
            skLineSegment(sketch, "E3.0.25.2", {"start": v(1.75, 26.25) * mm, "end": v(2.25, 26.25) * mm});
            skLineSegment(sketch, "E3.0.25.3", {"start": v(0.75, 25.75) * mm, "end": v(0.75, 26.25) * mm});
            skLineSegment(sketch, "E3.0.25.4", {"start": v(5.75, 26.25) * mm, "end": v(6.25, 26.25) * mm});
            skLineSegment(sketch, "E3.0.25.5", {"start": v(5.25, 25.75) * mm, "end": v(5.25, 26.25) * mm});
            skLineSegment(sketch, "E3.0.25.6", {"start": v(7.75, 25.75) * mm, "end": v(7.75, 26.25) * mm});
            skLineSegment(sketch, "E3.0.25.7", {"start": v(6.75, 25.75) * mm, "end": v(7.25, 25.75) * mm});
            skLineSegment(sketch, "E3.0.25.8", {"start": v(2.75, 25.75) * mm, "end": v(3.25, 25.75) * mm});
            skLineSegment(sketch, "E3.0.25.9", {"start": v(1.75, 25.75) * mm, "end": v(1.75, 26.25) * mm});
            skLineSegment(sketch, "E3.0.25.10", {"start": v(8.75, 25.75) * mm, "end": v(8.75, 26.25) * mm});
            skLineSegment(sketch, "E3.0.25.11", {"start": v(5.75, 25.75) * mm, "end": v(5.75, 26.25) * mm});
            skLineSegment(sketch, "E3.0.25.12", {"start": v(7.25, 25.75) * mm, "end": v(7.25, 26.25) * mm});
            skLineSegment(sketch, "E3.0.25.13", {"start": v(4.25, 25.75) * mm, "end": v(4.25, 26.25) * mm});
            skLineSegment(sketch, "E3.0.25.14", {"start": v(7.75, 26.25) * mm, "end": v(8.25, 26.25) * mm});
            skLineSegment(sketch, "E3.0.25.15", {"start": v(3.75, 25.75) * mm, "end": v(3.75, 26.25) * mm});
            skLineSegment(sketch, "E3.0.25.16", {"start": v(0.75, 26.25) * mm, "end": v(1.25, 26.25) * mm});
            skLineSegment(sketch, "E3.0.25.17", {"start": v(3.75, 25.75) * mm, "end": v(4.25, 25.75) * mm});
            skLineSegment(sketch, "E3.0.25.18", {"start": v(3.75, 26.25) * mm, "end": v(4.25, 26.25) * mm});
            skLineSegment(sketch, "E3.0.25.19", {"start": v(4.75, 25.75) * mm, "end": v(5.25, 25.75) * mm});
            skLineSegment(sketch, "E3.0.25.20", {"start": v(3.25, 25.75) * mm, "end": v(3.25, 26.25) * mm});
            skLineSegment(sketch, "E3.0.25.21", {"start": v(8.75, 25.75) * mm, "end": v(9.25, 25.75) * mm});
            skLineSegment(sketch, "E3.0.25.22", {"start": v(4.75, 26.25) * mm, "end": v(5.25, 26.25) * mm});
            skLineSegment(sketch, "E3.0.25.23", {"start": v(8.75, 26.25) * mm, "end": v(9.25, 26.25) * mm});
            skLineSegment(sketch, "E3.0.25.24", {"start": v(6.75, 25.75) * mm, "end": v(6.75, 26.25) * mm});
            skLineSegment(sketch, "E3.0.25.25", {"start": v(2.75, 25.75) * mm, "end": v(2.75, 26.25) * mm});
            skLineSegment(sketch, "E3.0.25.26", {"start": v(0.75, 25.75) * mm, "end": v(1.75, 25.75) * mm, "construction": true});
            skLineSegment(sketch, "E3.0.25.27", {"start": v(6.25, 25.75) * mm, "end": v(6.25, 26.25) * mm});
            skLineSegment(sketch, "E3.0.25.28", {"start": v(6.75, 26.25) * mm, "end": v(7.25, 26.25) * mm});
            skLineSegment(sketch, "E3.0.25.29", {"start": v(2.25, 25.75) * mm, "end": v(2.25, 26.25) * mm});
            skLineSegment(sketch, "E3.0.25.30", {"start": v(8.25, 25.75) * mm, "end": v(8.25, 26.25) * mm});
            skLineSegment(sketch, "E3.0.25.31", {"start": v(1.75, 25.75) * mm, "end": v(2.25, 25.75) * mm});
            skLineSegment(sketch, "E3.0.25.32", {"start": v(9.25, 25.75) * mm, "end": v(9.25, 26.25) * mm});
            skLineSegment(sketch, "E3.0.25.33", {"start": v(7.75, 25.75) * mm, "end": v(8.25, 25.75) * mm});
            skLineSegment(sketch, "E3.0.25.34", {"start": v(5.75, 25.75) * mm, "end": v(6.25, 25.75) * mm});
            skLineSegment(sketch, "E3.0.25.35", {"start": v(4.75, 25.75) * mm, "end": v(4.75, 26.25) * mm});
            skLineSegment(sketch, "E3.0.25.36", {"start": v(0.75, 25.75) * mm, "end": v(1.25, 25.75) * mm});
            skLineSegment(sketch, "E3.0.26.0", {"start": v(2.75, 27.25) * mm, "end": v(3.25, 27.25) * mm});
            skLineSegment(sketch, "E3.0.26.1", {"start": v(1.25, 26.75) * mm, "end": v(1.25, 27.25) * mm});
            skLineSegment(sketch, "E3.0.26.2", {"start": v(1.75, 27.25) * mm, "end": v(2.25, 27.25) * mm});
            skLineSegment(sketch, "E3.0.26.3", {"start": v(0.75, 26.75) * mm, "end": v(0.75, 27.25) * mm});
            skLineSegment(sketch, "E3.0.26.4", {"start": v(5.75, 27.25) * mm, "end": v(6.25, 27.25) * mm});
            skLineSegment(sketch, "E3.0.26.5", {"start": v(5.25, 26.75) * mm, "end": v(5.25, 27.25) * mm});
            skLineSegment(sketch, "E3.0.26.6", {"start": v(7.75, 26.75) * mm, "end": v(7.75, 27.25) * mm});
            skLineSegment(sketch, "E3.0.26.7", {"start": v(6.75, 26.75) * mm, "end": v(7.25, 26.75) * mm});
            skLineSegment(sketch, "E3.0.26.8", {"start": v(2.75, 26.75) * mm, "end": v(3.25, 26.75) * mm});
            skLineSegment(sketch, "E3.0.26.9", {"start": v(1.75, 26.75) * mm, "end": v(1.75, 27.25) * mm});
            skLineSegment(sketch, "E3.0.26.10", {"start": v(8.75, 26.75) * mm, "end": v(8.75, 27.25) * mm});
            skLineSegment(sketch, "E3.0.26.11", {"start": v(5.75, 26.75) * mm, "end": v(5.75, 27.25) * mm});
            skLineSegment(sketch, "E3.0.26.12", {"start": v(7.25, 26.75) * mm, "end": v(7.25, 27.25) * mm});
            skLineSegment(sketch, "E3.0.26.13", {"start": v(4.25, 26.75) * mm, "end": v(4.25, 27.25) * mm});
            skLineSegment(sketch, "E3.0.26.14", {"start": v(7.75, 27.25) * mm, "end": v(8.25, 27.25) * mm});
            skLineSegment(sketch, "E3.0.26.15", {"start": v(3.75, 26.75) * mm, "end": v(3.75, 27.25) * mm});
            skLineSegment(sketch, "E3.0.26.16", {"start": v(0.75, 27.25) * mm, "end": v(1.25, 27.25) * mm});
            skLineSegment(sketch, "E3.0.26.17", {"start": v(3.75, 26.75) * mm, "end": v(4.25, 26.75) * mm});
            skLineSegment(sketch, "E3.0.26.18", {"start": v(3.75, 27.25) * mm, "end": v(4.25, 27.25) * mm});
            skLineSegment(sketch, "E3.0.26.19", {"start": v(4.75, 26.75) * mm, "end": v(5.25, 26.75) * mm});
            skLineSegment(sketch, "E3.0.26.20", {"start": v(3.25, 26.75) * mm, "end": v(3.25, 27.25) * mm});
            skLineSegment(sketch, "E3.0.26.21", {"start": v(8.75, 26.75) * mm, "end": v(9.25, 26.75) * mm});
            skLineSegment(sketch, "E3.0.26.22", {"start": v(4.75, 27.25) * mm, "end": v(5.25, 27.25) * mm});
            skLineSegment(sketch, "E3.0.26.23", {"start": v(8.75, 27.25) * mm, "end": v(9.25, 27.25) * mm});
            skLineSegment(sketch, "E3.0.26.24", {"start": v(6.75, 26.75) * mm, "end": v(6.75, 27.25) * mm});
            skLineSegment(sketch, "E3.0.26.25", {"start": v(2.75, 26.75) * mm, "end": v(2.75, 27.25) * mm});
            skLineSegment(sketch, "E3.0.26.26", {"start": v(0.75, 26.75) * mm, "end": v(1.75, 26.75) * mm, "construction": true});
            skLineSegment(sketch, "E3.0.26.27", {"start": v(6.25, 26.75) * mm, "end": v(6.25, 27.25) * mm});
            skLineSegment(sketch, "E3.0.26.28", {"start": v(6.75, 27.25) * mm, "end": v(7.25, 27.25) * mm});
            skLineSegment(sketch, "E3.0.26.29", {"start": v(2.25, 26.75) * mm, "end": v(2.25, 27.25) * mm});
            skLineSegment(sketch, "E3.0.26.30", {"start": v(8.25, 26.75) * mm, "end": v(8.25, 27.25) * mm});
            skLineSegment(sketch, "E3.0.26.31", {"start": v(1.75, 26.75) * mm, "end": v(2.25, 26.75) * mm});
            skLineSegment(sketch, "E3.0.26.32", {"start": v(9.25, 26.75) * mm, "end": v(9.25, 27.25) * mm});
            skLineSegment(sketch, "E3.0.26.33", {"start": v(7.75, 26.75) * mm, "end": v(8.25, 26.75) * mm});
            skLineSegment(sketch, "E3.0.26.34", {"start": v(5.75, 26.75) * mm, "end": v(6.25, 26.75) * mm});
            skLineSegment(sketch, "E3.0.26.35", {"start": v(4.75, 26.75) * mm, "end": v(4.75, 27.25) * mm});
            skLineSegment(sketch, "E3.0.26.36", {"start": v(0.75, 26.75) * mm, "end": v(1.25, 26.75) * mm});
            skLineSegment(sketch, "E3.0.27.0", {"start": v(2.75, 28.25) * mm, "end": v(3.25, 28.25) * mm});
            skLineSegment(sketch, "E3.0.27.1", {"start": v(1.25, 27.75) * mm, "end": v(1.25, 28.25) * mm});
            skLineSegment(sketch, "E3.0.27.2", {"start": v(1.75, 28.25) * mm, "end": v(2.25, 28.25) * mm});
            skLineSegment(sketch, "E3.0.27.3", {"start": v(0.75, 27.75) * mm, "end": v(0.75, 28.25) * mm});
            skLineSegment(sketch, "E3.0.27.4", {"start": v(5.75, 28.25) * mm, "end": v(6.25, 28.25) * mm});
            skLineSegment(sketch, "E3.0.27.5", {"start": v(5.25, 27.75) * mm, "end": v(5.25, 28.25) * mm});
            skLineSegment(sketch, "E3.0.27.6", {"start": v(7.75, 27.75) * mm, "end": v(7.75, 28.25) * mm});
            skLineSegment(sketch, "E3.0.27.7", {"start": v(6.75, 27.75) * mm, "end": v(7.25, 27.75) * mm});
            skLineSegment(sketch, "E3.0.27.8", {"start": v(2.75, 27.75) * mm, "end": v(3.25, 27.75) * mm});
            skLineSegment(sketch, "E3.0.27.9", {"start": v(1.75, 27.75) * mm, "end": v(1.75, 28.25) * mm});
            skLineSegment(sketch, "E3.0.27.10", {"start": v(8.75, 27.75) * mm, "end": v(8.75, 28.25) * mm});
            skLineSegment(sketch, "E3.0.27.11", {"start": v(5.75, 27.75) * mm, "end": v(5.75, 28.25) * mm});
            skLineSegment(sketch, "E3.0.27.12", {"start": v(7.25, 27.75) * mm, "end": v(7.25, 28.25) * mm});
            skLineSegment(sketch, "E3.0.27.13", {"start": v(4.25, 27.75) * mm, "end": v(4.25, 28.25) * mm});
            skLineSegment(sketch, "E3.0.27.14", {"start": v(7.75, 28.25) * mm, "end": v(8.25, 28.25) * mm});
            skLineSegment(sketch, "E3.0.27.15", {"start": v(3.75, 27.75) * mm, "end": v(3.75, 28.25) * mm});
            skLineSegment(sketch, "E3.0.27.16", {"start": v(0.75, 28.25) * mm, "end": v(1.25, 28.25) * mm});
            skLineSegment(sketch, "E3.0.27.17", {"start": v(3.75, 27.75) * mm, "end": v(4.25, 27.75) * mm});
            skLineSegment(sketch, "E3.0.27.18", {"start": v(3.75, 28.25) * mm, "end": v(4.25, 28.25) * mm});
            skLineSegment(sketch, "E3.0.27.19", {"start": v(4.75, 27.75) * mm, "end": v(5.25, 27.75) * mm});
            skLineSegment(sketch, "E3.0.27.20", {"start": v(3.25, 27.75) * mm, "end": v(3.25, 28.25) * mm});
            skLineSegment(sketch, "E3.0.27.21", {"start": v(8.75, 27.75) * mm, "end": v(9.25, 27.75) * mm});
            skLineSegment(sketch, "E3.0.27.22", {"start": v(4.75, 28.25) * mm, "end": v(5.25, 28.25) * mm});
            skLineSegment(sketch, "E3.0.27.23", {"start": v(8.75, 28.25) * mm, "end": v(9.25, 28.25) * mm});
            skLineSegment(sketch, "E3.0.27.24", {"start": v(6.75, 27.75) * mm, "end": v(6.75, 28.25) * mm});
            skLineSegment(sketch, "E3.0.27.25", {"start": v(2.75, 27.75) * mm, "end": v(2.75, 28.25) * mm});
            skLineSegment(sketch, "E3.0.27.26", {"start": v(0.75, 27.75) * mm, "end": v(1.75, 27.75) * mm, "construction": true});
            skLineSegment(sketch, "E3.0.27.27", {"start": v(6.25, 27.75) * mm, "end": v(6.25, 28.25) * mm});
            skLineSegment(sketch, "E3.0.27.28", {"start": v(6.75, 28.25) * mm, "end": v(7.25, 28.25) * mm});
            skLineSegment(sketch, "E3.0.27.29", {"start": v(2.25, 27.75) * mm, "end": v(2.25, 28.25) * mm});
            skLineSegment(sketch, "E3.0.27.30", {"start": v(8.25, 27.75) * mm, "end": v(8.25, 28.25) * mm});
            skLineSegment(sketch, "E3.0.27.31", {"start": v(1.75, 27.75) * mm, "end": v(2.25, 27.75) * mm});
            skLineSegment(sketch, "E3.0.27.32", {"start": v(9.25, 27.75) * mm, "end": v(9.25, 28.25) * mm});
            skLineSegment(sketch, "E3.0.27.33", {"start": v(7.75, 27.75) * mm, "end": v(8.25, 27.75) * mm});
            skLineSegment(sketch, "E3.0.27.34", {"start": v(5.75, 27.75) * mm, "end": v(6.25, 27.75) * mm});
            skLineSegment(sketch, "E3.0.27.35", {"start": v(4.75, 27.75) * mm, "end": v(4.75, 28.25) * mm});
            skLineSegment(sketch, "E3.0.27.36", {"start": v(0.75, 27.75) * mm, "end": v(1.25, 27.75) * mm});
            skLineSegment(sketch, "E3.0.28.0", {"start": v(2.75, 29.25) * mm, "end": v(3.25, 29.25) * mm});
            skLineSegment(sketch, "E3.0.28.1", {"start": v(1.25, 28.75) * mm, "end": v(1.25, 29.25) * mm});
            skLineSegment(sketch, "E3.0.28.2", {"start": v(1.75, 29.25) * mm, "end": v(2.25, 29.25) * mm});
            skLineSegment(sketch, "E3.0.28.3", {"start": v(0.75, 28.75) * mm, "end": v(0.75, 29.25) * mm});
            skLineSegment(sketch, "E3.0.28.4", {"start": v(5.75, 29.25) * mm, "end": v(6.25, 29.25) * mm});
            skLineSegment(sketch, "E3.0.28.5", {"start": v(5.25, 28.75) * mm, "end": v(5.25, 29.25) * mm});
            skLineSegment(sketch, "E3.0.28.6", {"start": v(7.75, 28.75) * mm, "end": v(7.75, 29.25) * mm});
            skLineSegment(sketch, "E3.0.28.7", {"start": v(6.75, 28.75) * mm, "end": v(7.25, 28.75) * mm});
            skLineSegment(sketch, "E3.0.28.8", {"start": v(2.75, 28.75) * mm, "end": v(3.25, 28.75) * mm});
            skLineSegment(sketch, "E3.0.28.9", {"start": v(1.75, 28.75) * mm, "end": v(1.75, 29.25) * mm});
            skLineSegment(sketch, "E3.0.28.10", {"start": v(8.75, 28.75) * mm, "end": v(8.75, 29.25) * mm});
            skLineSegment(sketch, "E3.0.28.11", {"start": v(5.75, 28.75) * mm, "end": v(5.75, 29.25) * mm});
            skLineSegment(sketch, "E3.0.28.12", {"start": v(7.25, 28.75) * mm, "end": v(7.25, 29.25) * mm});
            skLineSegment(sketch, "E3.0.28.13", {"start": v(4.25, 28.75) * mm, "end": v(4.25, 29.25) * mm});
            skLineSegment(sketch, "E3.0.28.14", {"start": v(7.75, 29.25) * mm, "end": v(8.25, 29.25) * mm});
            skLineSegment(sketch, "E3.0.28.15", {"start": v(3.75, 28.75) * mm, "end": v(3.75, 29.25) * mm});
            skLineSegment(sketch, "E3.0.28.16", {"start": v(0.75, 29.25) * mm, "end": v(1.25, 29.25) * mm});
            skLineSegment(sketch, "E3.0.28.17", {"start": v(3.75, 28.75) * mm, "end": v(4.25, 28.75) * mm});
            skLineSegment(sketch, "E3.0.28.18", {"start": v(3.75, 29.25) * mm, "end": v(4.25, 29.25) * mm});
            skLineSegment(sketch, "E3.0.28.19", {"start": v(4.75, 28.75) * mm, "end": v(5.25, 28.75) * mm});
            skLineSegment(sketch, "E3.0.28.20", {"start": v(3.25, 28.75) * mm, "end": v(3.25, 29.25) * mm});
            skLineSegment(sketch, "E3.0.28.21", {"start": v(8.75, 28.75) * mm, "end": v(9.25, 28.75) * mm});
            skLineSegment(sketch, "E3.0.28.22", {"start": v(4.75, 29.25) * mm, "end": v(5.25, 29.25) * mm});
            skLineSegment(sketch, "E3.0.28.23", {"start": v(8.75, 29.25) * mm, "end": v(9.25, 29.25) * mm});
            skLineSegment(sketch, "E3.0.28.24", {"start": v(6.75, 28.75) * mm, "end": v(6.75, 29.25) * mm});
            skLineSegment(sketch, "E3.0.28.25", {"start": v(2.75, 28.75) * mm, "end": v(2.75, 29.25) * mm});
            skLineSegment(sketch, "E3.0.28.26", {"start": v(0.75, 28.75) * mm, "end": v(1.75, 28.75) * mm, "construction": true});
            skLineSegment(sketch, "E3.0.28.27", {"start": v(6.25, 28.75) * mm, "end": v(6.25, 29.25) * mm});
            skLineSegment(sketch, "E3.0.28.28", {"start": v(6.75, 29.25) * mm, "end": v(7.25, 29.25) * mm});
            skLineSegment(sketch, "E3.0.28.29", {"start": v(2.25, 28.75) * mm, "end": v(2.25, 29.25) * mm});
            skLineSegment(sketch, "E3.0.28.30", {"start": v(8.25, 28.75) * mm, "end": v(8.25, 29.25) * mm});
            skLineSegment(sketch, "E3.0.28.31", {"start": v(1.75, 28.75) * mm, "end": v(2.25, 28.75) * mm});
            skLineSegment(sketch, "E3.0.28.32", {"start": v(9.25, 28.75) * mm, "end": v(9.25, 29.25) * mm});
            skLineSegment(sketch, "E3.0.28.33", {"start": v(7.75, 28.75) * mm, "end": v(8.25, 28.75) * mm});
            skLineSegment(sketch, "E3.0.28.34", {"start": v(5.75, 28.75) * mm, "end": v(6.25, 28.75) * mm});
            skLineSegment(sketch, "E3.0.28.35", {"start": v(4.75, 28.75) * mm, "end": v(4.75, 29.25) * mm});
            skLineSegment(sketch, "E3.0.28.36", {"start": v(0.75, 28.75) * mm, "end": v(1.25, 28.75) * mm});
            skLineSegment(sketch, "E3.direction1", {"start": v(0.75, 0.75) * mm, "end": v(25.75, 0.75) * mm, "construction": true});
            skLineSegment(sketch, "E3.direction2", {"start": v(0.75, 0.75) * mm, "end": v(0.75, 1.75) * mm, "construction": true});
            skSolve(sketch);
        }
        {
            var Q0;
            Q0=qCreatedBy(makeId("Front.planeOp"),FACE);
            var sketch = newSketch(context, id + "F1", { "sketchPlane" : qUnion([Q0])});
            skLineSegment(sketch, "E4.bottom", {"start": v(0, 0) * mm, "end": v(10, 0) * mm});
            skLineSegment(sketch, "E4.top", {"start": v(0, 30) * mm, "end": v(10, 30) * mm});
            skLineSegment(sketch, "E4.left", {"start": v(0, 0) * mm, "end": v(0, 30) * mm});
            skLineSegment(sketch, "E4.right", {"start": v(10, 0) * mm, "end": v(10, 30) * mm});
            skSolve(sketch);
        }
        {
            var Q0;
            Q0 = qSketchRegion(id + "F1", true);
            extrude(context, id + "F2", {"entities" : qUnion([Q0]), "oppositeDirection" : true, "depth" : 10 * mm, "offsetDistance" : 25 * mm});
        }
        {
            var Q0;
            Q0 = qSketchRegion(id + "F0", true);
            extrude(context, id + "F3", {"entities" : qUnion([Q0]), "operationType" : NewBodyOperationType.ADD, "depth" : .5 * mm, "offsetDistance" : 25 * mm});
        }
    });
